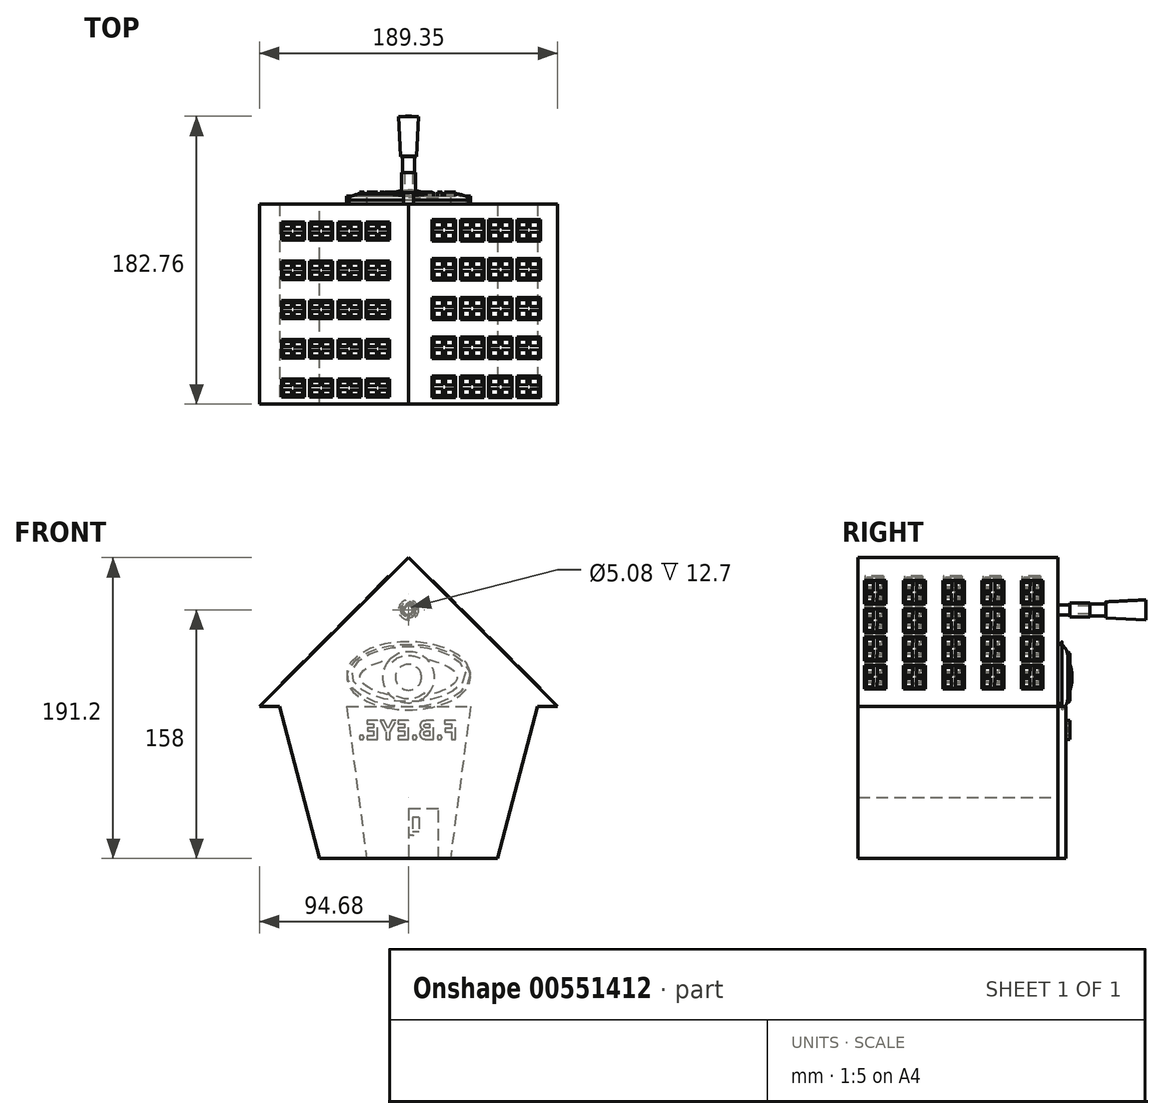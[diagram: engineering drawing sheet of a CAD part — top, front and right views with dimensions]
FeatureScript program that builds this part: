
annotation { "Feature Type Name" : "Feature", "Feature Type Description" : "" }
export const myFeature = defineFeature(function(context is Context, id is Id, definition is map)
    precondition{}
    {
        {
            var Q0;
            Q0=qCreatedBy(makeId("Front.planeOp"),FACE);
            var sketch = newSketch(context, id + "F0", { "sketchPlane" : qUnion([Q0])});
            skLineSegment(sketch, "E0.bottom", {"start": v(-42.95, 48.23) * mm, "end": v(35.63, 48.23) * mm});
            skLineSegment(sketch, "E1.top", {"start": v(-30.23, -48.3) * mm, "end": v(22.9, -48.3) * mm});
            skLineSegment(sketch, "E2", {"start": v(35.63, 48.23) * mm, "end": v(22.9, -48.3) * mm});
            skLineSegment(sketch, "E3", {"start": v(-42.95, 48.23) * mm, "end": v(-30.23, -48.3) * mm});
            skLineSegment(sketch, "E4", {"start": v(-42.95, 48.23) * mm, "end": v(22.9, -48.3) * mm, "construction": true});
            skLineSegment(sketch, "E5", {"start": v(-30.23, -48.3) * mm, "end": v(35.63, 48.23) * mm, "construction": true});
            skLineSegment(sketch, "E6", {"start": v(-3.66, -48.3) * mm, "end": v(-3.66, 48.23) * mm, "construction": true});
            skLineSegment(sketch, "E7", {"start": v(-3.66, 68.9) * mm, "end": v(12.85, 68.9) * mm, "construction": true});
            skCircle(sketch, "E8", {"center": v(-3.66, 68.9) * mm, "radius": 16.51 * mm});
            skLineSegment(sketch, "E9", {"start": v(-42.95, 48.23) * mm, "end": v(-42.95, 68.9) * mm, "construction": true});
            skLineSegment(sketch, "E10", {"start": v(35.63, 48.23) * mm, "end": v(35.63, 68.9) * mm, "construction": true});
            skEllipse(sketch, "E11", {"center": v(-3.66, 68.9) * mm, "majorRadius": 39.29 * mm, "minorRadius": 20.66 * mm, "majorAxis": v(1, 0)});
            skPoint(sketch, "E12", {"position": v(4.6, 68.9) * mm});
            skCircle(sketch, "E13", {"center": v(-3.66, 68.9) * mm, "radius": 8.26 * mm});
            skLineSegment(sketch, "E14", {"start": v(-3.66, 68.9) * mm, "end": v(-3.66, 66.88) * mm, "construction": true});
            skSolve(sketch);
        }
        {
            var Q0;
            Q0=makeQuery(id+"F0.imprint","IMPRINT",FACE,{"disambiguationData":[TD([[makeQuery(id+"F0.imprint","IMPRINT",EDGE,{"derivedFrom":sQuery(id+"F0.wireOp",EDGE,"E8")}),-1.0]])]});
            extrude(context, id + "F1", {"entities" : qUnion([Q0]), "oppositeDirection" : true, "depth" : 3.8 * mm, "offsetDistance" : 25.4 * mm});
        }
        {
            var Q0;
            Q0=makeQuery(id+"F0.imprint","IMPRINT",FACE,{"disambiguationData":[TD([[makeQuery(id+"F0.imprint","IMPRINT",EDGE,{"derivedFrom":sQuery(id+"F0.wireOp",EDGE,"E8")}),1.0]])]});
            extrude(context, id + "F2", {"entities" : qUnion([Q0]), "operationType" : NewBodyOperationType.ADD, "oppositeDirection" : true, "depth" : 5.08 * mm, "offsetDistance" : 25.4 * mm});
        }
        {
            var Q0;
            Q0=makeQuery(id+"F1.opExtrude","CAP_EDGE",EDGE,{"disambiguationData":[OSD([sQuery(id+"F0.wireOp",EDGE,"E11")])],"isStart":false});
            fillet(context, id + "F3", {"entities" : qUnion([Q0]), "radius" : 10.74 * mm, "tangentPropagation" : true, "allowEdgeOverflow" : false});
        }
        {
            var Q0;
            Q0=makeQuery(id+"F2.opExtrude","CAP_EDGE",EDGE,{"disambiguationData":[OSD([sQuery(id+"F0.wireOp",EDGE,"E8")])],"isStart":false});
            fillet(context, id + "F4", {"entities" : qUnion([Q0]), "radius" : 2.72 * mm, "tangentPropagation" : true, "allowEdgeOverflow" : false});
        }
        {
            var Q0;
            Q0=makeQuery(id+"F0.imprint","IMPRINT",FACE,{"disambiguationData":[TD([[makeQuery(id+"F0.imprint","IMPRINT",EDGE,{"derivedFrom":sQuery(id+"F0.wireOp",EDGE,"E13")}),1.0]])]});
            extrude(context, id + "F5", {"entities" : qUnion([Q0]), "operationType" : NewBodyOperationType.ADD, "oppositeDirection" : true, "depth" : 6.33 * mm, "offsetDistance" : 25.4 * mm});
        }
        {
            var Q0;
            Q0=makeQuery(id+"F5.opExtrude","CAP_FACE",FACE,{"disambiguationData":[OSD([sQuery(id+"F0.wireOp",EDGE,"E13")])],"isStart":false});
            fillet(context, id + "F6", {"entities" : qUnion([Q0]), "radius" : 26.1 * mm, "tangentPropagation" : true, "allowEdgeOverflow" : false});
        }
        {
            var Q0;
            Q0=makeQuery(id+"F0.imprint","IMPRINT",FACE,{"disambiguationData":[TD([[makeQuery(id+"F0.imprint","IMPRINT",EDGE,{"derivedFrom":sQuery(id+"F0.wireOp",EDGE,"E1.top")}),1.0]])]});
            extrude(context, id + "F7", {"entities" : qUnion([Q0]), "oppositeDirection" : true, "depth" : 5.08 * mm, "offsetDistance" : 25.4 * mm, "symmetric" : true});
        }
        {
            var Q0;
            Q0=makeQuery(id+"F0.imprint","IMPRINT",FACE,{"disambiguationData":[TD([[makeQuery(id+"F0.imprint","IMPRINT",EDGE,{"derivedFrom":sQuery(id+"F0.wireOp",EDGE,"E8")}),-1.0]])]});
            var Q1;
            Q1=makeQuery(id+"F0.imprint","IMPRINT",FACE,{"disambiguationData":[TD([[makeQuery(id+"F0.imprint","IMPRINT",EDGE,{"derivedFrom":sQuery(id+"F0.wireOp",EDGE,"E13")}),1.0]])]});
            var Q2;
            Q2=makeQuery(id+"F0.imprint","IMPRINT",FACE,{"disambiguationData":[TD([[makeQuery(id+"F0.imprint","IMPRINT",EDGE,{"derivedFrom":sQuery(id+"F0.wireOp",EDGE,"E8")}),1.0]])]});
            extrude(context, id + "F8", {"entities" : qUnion([Q0, Q1, Q2]), "depth" : 3.8 * mm, "offsetDistance" : 25.4 * mm});
        }
        {
            var Q0;
            Q0=makeQuery(id+"F8.opExtrude","CAP_EDGE",EDGE,{"disambiguationData":[OSD([sQuery(id+"F0.wireOp",EDGE,"E11")])],"isStart":false});
            fillet(context, id + "F9", {"entities" : qUnion([Q0]), "radius" : 10.33 * mm, "tangentPropagation" : true, "allowEdgeOverflow" : false});
        }
        {
            var Q0;
            Q0=makeQuery(id+"F1.opExtrude","SWEPT_BODY",BODY,{"disambiguationData":[OSD([sQuery(id+"F0.wireOp",EDGE,"E8"),sQuery(id+"F0.wireOp",EDGE,"E11")])]});
            var Q1;
            Q1=sQuery(id+"F0.wireOp",EDGE,"E14");
            transform(context, id + "F10", {"entities" : qUnion([Q0]), "transformType" : TransformType.TRANSLATION_ENTITY, "oppositeDirectionEntity" : false, "transformLine" : qUnion([Q1]), "makeCopy" : false});
        }
        {
            var Q0;
            Q0=makeQuery(id+"F7.opExtrude","CAP_FACE",FACE,{"disambiguationData":[OSD([sQuery(id+"F0.wireOp",EDGE,"E0.bottom"),sQuery(id+"F0.wireOp",EDGE,"E1.top"),sQuery(id+"F0.wireOp",EDGE,"E2"),sQuery(id+"F0.wireOp",EDGE,"E3")])],"isStart":false});
            var sketch = newSketch(context, id + "F11", { "sketchPlane" : qUnion([Q0])});
            skText(sketch, "E15", { "text": "F.B.EYE.", "fontName": "OpenSans-Bold.ttf"});
            const initialGuessF11  = {"E15": [-0.02755, 0.0275, 1, 0, 0.01194]};
            skSetInitialGuess(sketch, initialGuessF11);
            skSolve(sketch);
        }
        {
            var Q0;
            Q0=qSketchRegion(id+"F11",true);
            extrude(context, id + "F12", {"entities" : qUnion([Q0]), "operationType" : NewBodyOperationType.ADD, "depth" : 2.54 * mm, "offsetDistance" : 25.4 * mm});
        }
        {
            var Q0;
            Q0=makeQuery(id+"F7.opExtrude","CAP_FACE",FACE,{"disambiguationData":[OSD([sQuery(id+"F0.wireOp",EDGE,"E0.bottom"),sQuery(id+"F0.wireOp",EDGE,"E1.top"),sQuery(id+"F0.wireOp",EDGE,"E2"),sQuery(id+"F0.wireOp",EDGE,"E3")])],"isStart":true});
            var sketch = newSketch(context, id + "F13", { "sketchPlane" : qUnion([Q0])});
            skLineSegment(sketch, "E16.top", {"start": v(-85.64, -48.3) * mm, "end": v(78.31, -48.3) * mm});
            skLineSegment(sketch, "E16.left", {"start": v(-85.64, 48.23) * mm, "end": v(-85.64, -48.3) * mm});
            skLineSegment(sketch, "E16.right", {"start": v(78.31, 48.23) * mm, "end": v(78.31, -48.3) * mm});
            skPoint(sketch, "E17", {"position": v(-3.66, 43.57) * mm});
            skLineSegment(sketch, "E18.0", {"start": v(-42.95, 48.23) * mm, "end": v(22.9, -48.3) * mm});
            skLineSegment(sketch, "E19.0", {"start": v(-30.23, -48.3) * mm, "end": v(35.63, 48.23) * mm});
            skPoint(sketch, "E20", {"position": v(-3.66, -9.35) * mm});
            skLineSegment(sketch, "E21", {"start": v(-3.66, 43.57) * mm, "end": v(-3.66, -48.3) * mm});
            skLineSegment(sketch, "E22", {"start": v(-85.64, 48.23) * mm, "end": v(-98.34, 48.23) * mm});
            skLineSegment(sketch, "E23", {"start": v(-98.34, 48.23) * mm, "end": v(-3.66, 142.9) * mm});
            skLineSegment(sketch, "E24", {"start": v(-3.66, 142.9) * mm, "end": v(91.01, 48.23) * mm});
            skLineSegment(sketch, "E25", {"start": v(78.31, 48.23) * mm, "end": v(91.01, 48.23) * mm});
            skSolve(sketch);
        }
        {
            var Q0;
            Q0=qSketchRegion(id+"F13",true);
            extrude(context, id + "F14", {"entities" : qUnion([Q0]), "operationType" : NewBodyOperationType.ADD, "depth" : 127 * mm, "offsetDistance" : 25.4 * mm});
        }
        {
            var Q0;
            Q0=makeQuery(id+"F14.opExtrude","SWEPT_EDGE",EDGE,{"disambiguationData":[OSD([sQuery(id+"F13.wireOp",EDGE,"E16.top"),sQuery(id+"F13.wireOp",EDGE,"E16.left")])]});
            var Q1;
            Q1=makeQuery(id+"F14.opExtrude","SWEPT_EDGE",EDGE,{"disambiguationData":[OSD([sQuery(id+"F13.wireOp",EDGE,"E16.top"),sQuery(id+"F13.wireOp",EDGE,"E16.right")])]});
            chamfer(context, id + "F15", {"entities" : qUnion([Q0, Q1]), "chamferType" : ChamferType.OFFSET_ANGLE, "width" : 25.4 * mm, "oppositeDirection" : false, "angle" : 75.26 * degree, "tangentPropagation" : true});
        }
        {
            var Q0;
            Q0=makeQuery(id+"F14.opExtrude","SWEPT_FACE",FACE,{"disambiguationData":[OSD([sQuery(id+"F13.wireOp",EDGE,"E24")])]});
            var sketch = newSketch(context, id + "F16", { "sketchPlane" : qUnion([Q0])});
            skLineSegment(sketch, "E26.bottom", {"start": v(-124.24, 5.02) * mm, "end": v(-119.76, 5.02) * mm});
            skLineSegment(sketch, "E26.top", {"start": v(-124.24, -13.15) * mm, "end": v(-120.07, -13.15) * mm});
            skLineSegment(sketch, "E26.left", {"start": v(-124.24, 5.02) * mm, "end": v(-124.24, -2.98) * mm});
            skLineSegment(sketch, "E26.right", {"start": v(-113.04, 5.02) * mm, "end": v(-113.04, -2.98) * mm});
            skPoint(sketch, "E27", {"position": v(-118.64, -4.07) * mm});
            skPoint(sketch, "E27.positionSnap0", {"position": v(-113.04, -4.07) * mm});
            skPoint(sketch, "E27.positionSnap1", {"position": v(-118.64, -13.15) * mm});
            skLineSegment(sketch, "E28.left", {"start": v(-117.22, 5.02) * mm, "end": v(-117.36, -2.98) * mm});
            skLineSegment(sketch, "E28.right", {"start": v(-119.76, 5.02) * mm, "end": v(-119.9, -2.98) * mm});
            skLineSegment(sketch, "E29.bottom", {"start": v(-113.04, -5.15) * mm, "end": v(-117.4, -5.15) * mm});
            skLineSegment(sketch, "E29.top", {"start": v(-113.04, -2.98) * mm, "end": v(-117.36, -2.98) * mm});
            skLineSegment(sketch, "E30.0", {"start": v(-125.51, 6.29) * mm, "end": v(-111.77, 6.29) * mm});
            skLineSegment(sketch, "E30.1", {"start": v(-125.51, 6.29) * mm, "end": v(-125.51, -14.42) * mm});
            skLineSegment(sketch, "E30.2", {"start": v(-125.51, -14.42) * mm, "end": v(-111.77, -14.42) * mm});
            skLineSegment(sketch, "E30.3", {"start": v(-111.77, 6.29) * mm, "end": v(-111.77, -14.42) * mm});
            skLineSegment(sketch, "E31.trimOffspring", {"start": v(-119.9, -2.98) * mm, "end": v(-124.24, -2.98) * mm});
            skLineSegment(sketch, "E32.trimOffspring", {"start": v(-119.93, -5.15) * mm, "end": v(-120.07, -13.15) * mm});
            skLineSegment(sketch, "E33.trimOffspring", {"start": v(-119.93, -5.15) * mm, "end": v(-124.24, -5.15) * mm});
            skLineSegment(sketch, "E34.trimOffspring", {"start": v(-117.4, -5.15) * mm, "end": v(-117.53, -13.15) * mm});
            skLineSegment(sketch, "E35.trimOffspring", {"start": v(-113.04, -5.15) * mm, "end": v(-113.04, -13.15) * mm});
            skLineSegment(sketch, "E36.trimOffspring", {"start": v(-117.53, -13.15) * mm, "end": v(-113.04, -13.15) * mm});
            skLineSegment(sketch, "E37.trimOffspring", {"start": v(-124.24, -5.15) * mm, "end": v(-124.24, -13.15) * mm});
            skLineSegment(sketch, "E38.trimOffspring", {"start": v(-117.22, 5.02) * mm, "end": v(-113.04, 5.02) * mm});
            skPoint(sketch, "E39.0.1.0", {"position": v(-118.64, 21.33) * mm});
            skLineSegment(sketch, "E39.0.1.1", {"start": v(-117.22, 30.42) * mm, "end": v(-113.04, 30.42) * mm});
            skLineSegment(sketch, "E39.0.1.2", {"start": v(-113.04, 20.25) * mm, "end": v(-113.04, 12.25) * mm});
            skLineSegment(sketch, "E39.0.1.3", {"start": v(-117.53, 12.25) * mm, "end": v(-113.04, 12.25) * mm});
            skLineSegment(sketch, "E39.0.1.4", {"start": v(-125.51, 10.98) * mm, "end": v(-111.77, 10.98) * mm});
            skLineSegment(sketch, "E39.0.1.5", {"start": v(-125.51, 31.69) * mm, "end": v(-125.51, 10.98) * mm});
            skLineSegment(sketch, "E39.0.1.6", {"start": v(-113.04, 22.42) * mm, "end": v(-117.36, 22.42) * mm});
            skLineSegment(sketch, "E39.0.1.7", {"start": v(-113.04, 20.25) * mm, "end": v(-117.4, 20.25) * mm});
            skLineSegment(sketch, "E39.0.1.8", {"start": v(-119.76, 30.42) * mm, "end": v(-119.9, 22.42) * mm});
            skLineSegment(sketch, "E39.0.1.9", {"start": v(-117.22, 30.42) * mm, "end": v(-117.36, 22.42) * mm});
            skLineSegment(sketch, "E39.0.1.10", {"start": v(-113.04, 30.42) * mm, "end": v(-113.04, 22.42) * mm});
            skLineSegment(sketch, "E39.0.1.11", {"start": v(-124.24, 30.42) * mm, "end": v(-124.24, 22.42) * mm});
            skLineSegment(sketch, "E39.0.1.12", {"start": v(-124.24, 12.25) * mm, "end": v(-120.07, 12.25) * mm});
            skLineSegment(sketch, "E39.0.1.13", {"start": v(-124.24, 30.42) * mm, "end": v(-119.76, 30.42) * mm});
            skLineSegment(sketch, "E39.0.1.14", {"start": v(-117.4, 20.25) * mm, "end": v(-117.53, 12.25) * mm});
            skLineSegment(sketch, "E39.0.1.15", {"start": v(-119.93, 20.25) * mm, "end": v(-124.24, 20.25) * mm});
            skLineSegment(sketch, "E39.0.1.16", {"start": v(-119.93, 20.25) * mm, "end": v(-120.07, 12.25) * mm});
            skLineSegment(sketch, "E39.0.1.17", {"start": v(-125.51, 31.69) * mm, "end": v(-111.77, 31.69) * mm});
            skLineSegment(sketch, "E39.0.1.18", {"start": v(-111.77, 31.69) * mm, "end": v(-111.77, 10.98) * mm});
            skLineSegment(sketch, "E39.0.1.19", {"start": v(-119.9, 22.42) * mm, "end": v(-124.24, 22.42) * mm});
            skPoint(sketch, "E39.0.1.20", {"position": v(-113.04, 21.33) * mm});
            skPoint(sketch, "E39.0.1.21", {"position": v(-118.64, 12.25) * mm});
            skLineSegment(sketch, "E39.0.1.22", {"start": v(-124.24, 20.25) * mm, "end": v(-124.24, 12.25) * mm});
            skPoint(sketch, "E39.0.1.23", {"position": v(-118.64, 21.33) * mm});
            skPoint(sketch, "E39.0.1.24", {"position": v(-118.64, 21.33) * mm});
            skPoint(sketch, "E39.0.2.0", {"position": v(-118.64, 46.73) * mm});
            skLineSegment(sketch, "E39.0.2.1", {"start": v(-117.22, 55.82) * mm, "end": v(-113.04, 55.82) * mm});
            skLineSegment(sketch, "E39.0.2.2", {"start": v(-113.04, 45.65) * mm, "end": v(-113.04, 37.65) * mm});
            skLineSegment(sketch, "E39.0.2.3", {"start": v(-117.53, 37.65) * mm, "end": v(-113.04, 37.65) * mm});
            skLineSegment(sketch, "E39.0.2.4", {"start": v(-125.51, 36.38) * mm, "end": v(-111.77, 36.38) * mm});
            skLineSegment(sketch, "E39.0.2.5", {"start": v(-125.51, 57.09) * mm, "end": v(-125.51, 36.38) * mm});
            skLineSegment(sketch, "E39.0.2.6", {"start": v(-113.04, 47.82) * mm, "end": v(-117.36, 47.82) * mm});
            skLineSegment(sketch, "E39.0.2.7", {"start": v(-113.04, 45.65) * mm, "end": v(-117.4, 45.65) * mm});
            skLineSegment(sketch, "E39.0.2.8", {"start": v(-119.76, 55.82) * mm, "end": v(-119.9, 47.82) * mm});
            skLineSegment(sketch, "E39.0.2.9", {"start": v(-117.22, 55.82) * mm, "end": v(-117.36, 47.82) * mm});
            skLineSegment(sketch, "E39.0.2.10", {"start": v(-113.04, 55.82) * mm, "end": v(-113.04, 47.82) * mm});
            skLineSegment(sketch, "E39.0.2.11", {"start": v(-124.24, 55.82) * mm, "end": v(-124.24, 47.82) * mm});
            skLineSegment(sketch, "E39.0.2.12", {"start": v(-124.24, 37.65) * mm, "end": v(-120.07, 37.65) * mm});
            skLineSegment(sketch, "E39.0.2.13", {"start": v(-124.24, 55.82) * mm, "end": v(-119.76, 55.82) * mm});
            skLineSegment(sketch, "E39.0.2.14", {"start": v(-117.4, 45.65) * mm, "end": v(-117.53, 37.65) * mm});
            skLineSegment(sketch, "E39.0.2.15", {"start": v(-119.93, 45.65) * mm, "end": v(-124.24, 45.65) * mm});
            skLineSegment(sketch, "E39.0.2.16", {"start": v(-119.93, 45.65) * mm, "end": v(-120.07, 37.65) * mm});
            skLineSegment(sketch, "E39.0.2.17", {"start": v(-125.51, 57.09) * mm, "end": v(-111.77, 57.09) * mm});
            skLineSegment(sketch, "E39.0.2.18", {"start": v(-111.77, 57.09) * mm, "end": v(-111.77, 36.38) * mm});
            skLineSegment(sketch, "E39.0.2.19", {"start": v(-119.9, 47.82) * mm, "end": v(-124.24, 47.82) * mm});
            skPoint(sketch, "E39.0.2.20", {"position": v(-113.04, 46.73) * mm});
            skPoint(sketch, "E39.0.2.21", {"position": v(-118.64, 37.65) * mm});
            skLineSegment(sketch, "E39.0.2.22", {"start": v(-124.24, 45.65) * mm, "end": v(-124.24, 37.65) * mm});
            skPoint(sketch, "E39.0.2.23", {"position": v(-118.64, 46.73) * mm});
            skPoint(sketch, "E39.0.2.24", {"position": v(-118.64, 46.73) * mm});
            skPoint(sketch, "E39.0.3.0", {"position": v(-118.64, 72.13) * mm});
            skLineSegment(sketch, "E39.0.3.1", {"start": v(-117.22, 81.22) * mm, "end": v(-113.04, 81.22) * mm});
            skLineSegment(sketch, "E39.0.3.2", {"start": v(-113.04, 71.05) * mm, "end": v(-113.04, 63.05) * mm});
            skLineSegment(sketch, "E39.0.3.3", {"start": v(-117.53, 63.05) * mm, "end": v(-113.04, 63.05) * mm});
            skLineSegment(sketch, "E39.0.3.4", {"start": v(-125.51, 61.78) * mm, "end": v(-111.77, 61.78) * mm});
            skLineSegment(sketch, "E39.0.3.5", {"start": v(-125.51, 82.49) * mm, "end": v(-125.51, 61.78) * mm});
            skLineSegment(sketch, "E39.0.3.6", {"start": v(-113.04, 73.22) * mm, "end": v(-117.36, 73.22) * mm});
            skLineSegment(sketch, "E39.0.3.7", {"start": v(-113.04, 71.05) * mm, "end": v(-117.4, 71.05) * mm});
            skLineSegment(sketch, "E39.0.3.8", {"start": v(-119.76, 81.22) * mm, "end": v(-119.9, 73.22) * mm});
            skLineSegment(sketch, "E39.0.3.9", {"start": v(-117.22, 81.22) * mm, "end": v(-117.36, 73.22) * mm});
            skLineSegment(sketch, "E39.0.3.10", {"start": v(-113.04, 81.22) * mm, "end": v(-113.04, 73.22) * mm});
            skLineSegment(sketch, "E39.0.3.11", {"start": v(-124.24, 81.22) * mm, "end": v(-124.24, 73.22) * mm});
            skLineSegment(sketch, "E39.0.3.12", {"start": v(-124.24, 63.05) * mm, "end": v(-120.07, 63.05) * mm});
            skLineSegment(sketch, "E39.0.3.13", {"start": v(-124.24, 81.22) * mm, "end": v(-119.76, 81.22) * mm});
            skLineSegment(sketch, "E39.0.3.14", {"start": v(-117.4, 71.05) * mm, "end": v(-117.53, 63.05) * mm});
            skLineSegment(sketch, "E39.0.3.15", {"start": v(-119.93, 71.05) * mm, "end": v(-124.24, 71.05) * mm});
            skLineSegment(sketch, "E39.0.3.16", {"start": v(-119.93, 71.05) * mm, "end": v(-120.07, 63.05) * mm});
            skLineSegment(sketch, "E39.0.3.17", {"start": v(-125.51, 82.49) * mm, "end": v(-111.77, 82.49) * mm});
            skLineSegment(sketch, "E39.0.3.18", {"start": v(-111.77, 82.49) * mm, "end": v(-111.77, 61.78) * mm});
            skLineSegment(sketch, "E39.0.3.19", {"start": v(-119.9, 73.22) * mm, "end": v(-124.24, 73.22) * mm});
            skPoint(sketch, "E39.0.3.20", {"position": v(-113.04, 72.13) * mm});
            skPoint(sketch, "E39.0.3.21", {"position": v(-118.64, 63.05) * mm});
            skLineSegment(sketch, "E39.0.3.22", {"start": v(-124.24, 71.05) * mm, "end": v(-124.24, 63.05) * mm});
            skPoint(sketch, "E39.0.3.23", {"position": v(-118.64, 72.13) * mm});
            skPoint(sketch, "E39.0.3.24", {"position": v(-118.64, 72.13) * mm});
            skPoint(sketch, "E39.1.0.0", {"position": v(-93.75, -4.07) * mm});
            skLineSegment(sketch, "E39.1.0.1", {"start": v(-92.33, 5.02) * mm, "end": v(-88.15, 5.02) * mm});
            skLineSegment(sketch, "E39.1.0.2", {"start": v(-88.15, -5.15) * mm, "end": v(-88.15, -13.15) * mm});
            skLineSegment(sketch, "E39.1.0.3", {"start": v(-92.64, -13.15) * mm, "end": v(-88.15, -13.15) * mm});
            skLineSegment(sketch, "E39.1.0.4", {"start": v(-100.62, -14.42) * mm, "end": v(-86.88, -14.42) * mm});
            skLineSegment(sketch, "E39.1.0.5", {"start": v(-100.62, 6.29) * mm, "end": v(-100.62, -14.42) * mm});
            skLineSegment(sketch, "E39.1.0.6", {"start": v(-88.15, -2.98) * mm, "end": v(-92.47, -2.98) * mm});
            skLineSegment(sketch, "E39.1.0.7", {"start": v(-88.15, -5.15) * mm, "end": v(-92.5, -5.15) * mm});
            skLineSegment(sketch, "E39.1.0.8", {"start": v(-94.87, 5.02) * mm, "end": v(-95, -2.98) * mm});
            skLineSegment(sketch, "E39.1.0.9", {"start": v(-92.33, 5.02) * mm, "end": v(-92.47, -2.98) * mm});
            skLineSegment(sketch, "E39.1.0.10", {"start": v(-88.15, 5.02) * mm, "end": v(-88.15, -2.98) * mm});
            skLineSegment(sketch, "E39.1.0.11", {"start": v(-99.35, 5.02) * mm, "end": v(-99.35, -2.98) * mm});
            skLineSegment(sketch, "E39.1.0.12", {"start": v(-99.35, -13.15) * mm, "end": v(-95.17, -13.15) * mm});
            skLineSegment(sketch, "E39.1.0.13", {"start": v(-99.35, 5.02) * mm, "end": v(-94.87, 5.02) * mm});
            skLineSegment(sketch, "E39.1.0.14", {"start": v(-92.5, -5.15) * mm, "end": v(-92.64, -13.15) * mm});
            skLineSegment(sketch, "E39.1.0.15", {"start": v(-95.04, -5.15) * mm, "end": v(-99.35, -5.15) * mm});
            skLineSegment(sketch, "E39.1.0.16", {"start": v(-95.04, -5.15) * mm, "end": v(-95.17, -13.15) * mm});
            skLineSegment(sketch, "E39.1.0.17", {"start": v(-100.62, 6.29) * mm, "end": v(-86.88, 6.29) * mm});
            skLineSegment(sketch, "E39.1.0.18", {"start": v(-86.88, 6.29) * mm, "end": v(-86.88, -14.42) * mm});
            skLineSegment(sketch, "E39.1.0.19", {"start": v(-95, -2.98) * mm, "end": v(-99.35, -2.98) * mm});
            skPoint(sketch, "E39.1.0.20", {"position": v(-88.15, -4.07) * mm});
            skPoint(sketch, "E39.1.0.21", {"position": v(-93.75, -13.15) * mm});
            skLineSegment(sketch, "E39.1.0.22", {"start": v(-99.35, -5.15) * mm, "end": v(-99.35, -13.15) * mm});
            skPoint(sketch, "E39.1.0.23", {"position": v(-93.75, -4.07) * mm});
            skPoint(sketch, "E39.1.0.24", {"position": v(-93.75, -4.07) * mm});
            skPoint(sketch, "E39.1.1.0", {"position": v(-93.75, 21.33) * mm});
            skLineSegment(sketch, "E39.1.1.1", {"start": v(-92.33, 30.42) * mm, "end": v(-88.15, 30.42) * mm});
            skLineSegment(sketch, "E39.1.1.2", {"start": v(-88.15, 20.25) * mm, "end": v(-88.15, 12.25) * mm});
            skLineSegment(sketch, "E39.1.1.3", {"start": v(-92.64, 12.25) * mm, "end": v(-88.15, 12.25) * mm});
            skLineSegment(sketch, "E39.1.1.4", {"start": v(-100.62, 10.98) * mm, "end": v(-86.88, 10.98) * mm});
            skLineSegment(sketch, "E39.1.1.5", {"start": v(-100.62, 31.69) * mm, "end": v(-100.62, 10.98) * mm});
            skLineSegment(sketch, "E39.1.1.6", {"start": v(-88.15, 22.42) * mm, "end": v(-92.47, 22.42) * mm});
            skLineSegment(sketch, "E39.1.1.7", {"start": v(-88.15, 20.25) * mm, "end": v(-92.5, 20.25) * mm});
            skLineSegment(sketch, "E39.1.1.8", {"start": v(-94.87, 30.42) * mm, "end": v(-95, 22.42) * mm});
            skLineSegment(sketch, "E39.1.1.9", {"start": v(-92.33, 30.42) * mm, "end": v(-92.47, 22.42) * mm});
            skLineSegment(sketch, "E39.1.1.10", {"start": v(-88.15, 30.42) * mm, "end": v(-88.15, 22.42) * mm});
            skLineSegment(sketch, "E39.1.1.11", {"start": v(-99.35, 30.42) * mm, "end": v(-99.35, 22.42) * mm});
            skLineSegment(sketch, "E39.1.1.12", {"start": v(-99.35, 12.25) * mm, "end": v(-95.17, 12.25) * mm});
            skLineSegment(sketch, "E39.1.1.13", {"start": v(-99.35, 30.42) * mm, "end": v(-94.87, 30.42) * mm});
            skLineSegment(sketch, "E39.1.1.14", {"start": v(-92.5, 20.25) * mm, "end": v(-92.64, 12.25) * mm});
            skLineSegment(sketch, "E39.1.1.15", {"start": v(-95.04, 20.25) * mm, "end": v(-99.35, 20.25) * mm});
            skLineSegment(sketch, "E39.1.1.16", {"start": v(-95.04, 20.25) * mm, "end": v(-95.17, 12.25) * mm});
            skLineSegment(sketch, "E39.1.1.17", {"start": v(-100.62, 31.69) * mm, "end": v(-86.88, 31.69) * mm});
            skLineSegment(sketch, "E39.1.1.18", {"start": v(-86.88, 31.69) * mm, "end": v(-86.88, 10.98) * mm});
            skLineSegment(sketch, "E39.1.1.19", {"start": v(-95, 22.42) * mm, "end": v(-99.35, 22.42) * mm});
            skPoint(sketch, "E39.1.1.20", {"position": v(-88.15, 21.33) * mm});
            skPoint(sketch, "E39.1.1.21", {"position": v(-93.75, 12.25) * mm});
            skLineSegment(sketch, "E39.1.1.22", {"start": v(-99.35, 20.25) * mm, "end": v(-99.35, 12.25) * mm});
            skPoint(sketch, "E39.1.1.23", {"position": v(-93.75, 21.33) * mm});
            skPoint(sketch, "E39.1.1.24", {"position": v(-93.75, 21.33) * mm});
            skPoint(sketch, "E39.1.2.0", {"position": v(-93.75, 46.73) * mm});
            skLineSegment(sketch, "E39.1.2.1", {"start": v(-92.33, 55.82) * mm, "end": v(-88.15, 55.82) * mm});
            skLineSegment(sketch, "E39.1.2.2", {"start": v(-88.15, 45.65) * mm, "end": v(-88.15, 37.65) * mm});
            skLineSegment(sketch, "E39.1.2.3", {"start": v(-92.64, 37.65) * mm, "end": v(-88.15, 37.65) * mm});
            skLineSegment(sketch, "E39.1.2.4", {"start": v(-100.62, 36.38) * mm, "end": v(-86.88, 36.38) * mm});
            skLineSegment(sketch, "E39.1.2.5", {"start": v(-100.62, 57.09) * mm, "end": v(-100.62, 36.38) * mm});
            skLineSegment(sketch, "E39.1.2.6", {"start": v(-88.15, 47.82) * mm, "end": v(-92.47, 47.82) * mm});
            skLineSegment(sketch, "E39.1.2.7", {"start": v(-88.15, 45.65) * mm, "end": v(-92.5, 45.65) * mm});
            skLineSegment(sketch, "E39.1.2.8", {"start": v(-94.87, 55.82) * mm, "end": v(-95, 47.82) * mm});
            skLineSegment(sketch, "E39.1.2.9", {"start": v(-92.33, 55.82) * mm, "end": v(-92.47, 47.82) * mm});
            skLineSegment(sketch, "E39.1.2.10", {"start": v(-88.15, 55.82) * mm, "end": v(-88.15, 47.82) * mm});
            skLineSegment(sketch, "E39.1.2.11", {"start": v(-99.35, 55.82) * mm, "end": v(-99.35, 47.82) * mm});
            skLineSegment(sketch, "E39.1.2.12", {"start": v(-99.35, 37.65) * mm, "end": v(-95.17, 37.65) * mm});
            skLineSegment(sketch, "E39.1.2.13", {"start": v(-99.35, 55.82) * mm, "end": v(-94.87, 55.82) * mm});
            skLineSegment(sketch, "E39.1.2.14", {"start": v(-92.5, 45.65) * mm, "end": v(-92.64, 37.65) * mm});
            skLineSegment(sketch, "E39.1.2.15", {"start": v(-95.04, 45.65) * mm, "end": v(-99.35, 45.65) * mm});
            skLineSegment(sketch, "E39.1.2.16", {"start": v(-95.04, 45.65) * mm, "end": v(-95.17, 37.65) * mm});
            skLineSegment(sketch, "E39.1.2.17", {"start": v(-100.62, 57.09) * mm, "end": v(-86.88, 57.09) * mm});
            skLineSegment(sketch, "E39.1.2.18", {"start": v(-86.88, 57.09) * mm, "end": v(-86.88, 36.38) * mm});
            skLineSegment(sketch, "E39.1.2.19", {"start": v(-95, 47.82) * mm, "end": v(-99.35, 47.82) * mm});
            skPoint(sketch, "E39.1.2.20", {"position": v(-88.15, 46.73) * mm});
            skPoint(sketch, "E39.1.2.21", {"position": v(-93.75, 37.65) * mm});
            skLineSegment(sketch, "E39.1.2.22", {"start": v(-99.35, 45.65) * mm, "end": v(-99.35, 37.65) * mm});
            skPoint(sketch, "E39.1.2.23", {"position": v(-93.75, 46.73) * mm});
            skPoint(sketch, "E39.1.2.24", {"position": v(-93.75, 46.73) * mm});
            skPoint(sketch, "E39.1.3.0", {"position": v(-93.75, 72.13) * mm});
            skLineSegment(sketch, "E39.1.3.1", {"start": v(-92.33, 81.22) * mm, "end": v(-88.15, 81.22) * mm});
            skLineSegment(sketch, "E39.1.3.2", {"start": v(-88.15, 71.05) * mm, "end": v(-88.15, 63.05) * mm});
            skLineSegment(sketch, "E39.1.3.3", {"start": v(-92.64, 63.05) * mm, "end": v(-88.15, 63.05) * mm});
            skLineSegment(sketch, "E39.1.3.4", {"start": v(-100.62, 61.78) * mm, "end": v(-86.88, 61.78) * mm});
            skLineSegment(sketch, "E39.1.3.5", {"start": v(-100.62, 82.49) * mm, "end": v(-100.62, 61.78) * mm});
            skLineSegment(sketch, "E39.1.3.6", {"start": v(-88.15, 73.22) * mm, "end": v(-92.47, 73.22) * mm});
            skLineSegment(sketch, "E39.1.3.7", {"start": v(-88.15, 71.05) * mm, "end": v(-92.5, 71.05) * mm});
            skLineSegment(sketch, "E39.1.3.8", {"start": v(-94.87, 81.22) * mm, "end": v(-95, 73.22) * mm});
            skLineSegment(sketch, "E39.1.3.9", {"start": v(-92.33, 81.22) * mm, "end": v(-92.47, 73.22) * mm});
            skLineSegment(sketch, "E39.1.3.10", {"start": v(-88.15, 81.22) * mm, "end": v(-88.15, 73.22) * mm});
            skLineSegment(sketch, "E39.1.3.11", {"start": v(-99.35, 81.22) * mm, "end": v(-99.35, 73.22) * mm});
            skLineSegment(sketch, "E39.1.3.12", {"start": v(-99.35, 63.05) * mm, "end": v(-95.17, 63.05) * mm});
            skLineSegment(sketch, "E39.1.3.13", {"start": v(-99.35, 81.22) * mm, "end": v(-94.87, 81.22) * mm});
            skLineSegment(sketch, "E39.1.3.14", {"start": v(-92.5, 71.05) * mm, "end": v(-92.64, 63.05) * mm});
            skLineSegment(sketch, "E39.1.3.15", {"start": v(-95.04, 71.05) * mm, "end": v(-99.35, 71.05) * mm});
            skLineSegment(sketch, "E39.1.3.16", {"start": v(-95.04, 71.05) * mm, "end": v(-95.17, 63.05) * mm});
            skLineSegment(sketch, "E39.1.3.17", {"start": v(-100.62, 82.49) * mm, "end": v(-86.88, 82.49) * mm});
            skLineSegment(sketch, "E39.1.3.18", {"start": v(-86.88, 82.49) * mm, "end": v(-86.88, 61.78) * mm});
            skLineSegment(sketch, "E39.1.3.19", {"start": v(-95, 73.22) * mm, "end": v(-99.35, 73.22) * mm});
            skPoint(sketch, "E39.1.3.20", {"position": v(-88.15, 72.13) * mm});
            skPoint(sketch, "E39.1.3.21", {"position": v(-93.75, 63.05) * mm});
            skLineSegment(sketch, "E39.1.3.22", {"start": v(-99.35, 71.05) * mm, "end": v(-99.35, 63.05) * mm});
            skPoint(sketch, "E39.1.3.23", {"position": v(-93.75, 72.13) * mm});
            skPoint(sketch, "E39.1.3.24", {"position": v(-93.75, 72.13) * mm});
            skPoint(sketch, "E39.2.0.0", {"position": v(-68.86, -4.07) * mm});
            skLineSegment(sketch, "E39.2.0.1", {"start": v(-67.44, 5.02) * mm, "end": v(-63.26, 5.02) * mm});
            skLineSegment(sketch, "E39.2.0.2", {"start": v(-63.26, -5.15) * mm, "end": v(-63.26, -13.15) * mm});
            skLineSegment(sketch, "E39.2.0.3", {"start": v(-67.75, -13.15) * mm, "end": v(-63.26, -13.15) * mm});
            skLineSegment(sketch, "E39.2.0.4", {"start": v(-75.73, -14.42) * mm, "end": v(-62, -14.42) * mm});
            skLineSegment(sketch, "E39.2.0.5", {"start": v(-75.73, 6.29) * mm, "end": v(-75.73, -14.42) * mm});
            skLineSegment(sketch, "E39.2.0.6", {"start": v(-63.26, -2.98) * mm, "end": v(-67.57, -2.98) * mm});
            skLineSegment(sketch, "E39.2.0.7", {"start": v(-63.26, -5.15) * mm, "end": v(-67.61, -5.15) * mm});
            skLineSegment(sketch, "E39.2.0.8", {"start": v(-69.97, 5.02) * mm, "end": v(-70.1, -2.98) * mm});
            skLineSegment(sketch, "E39.2.0.9", {"start": v(-67.44, 5.02) * mm, "end": v(-67.57, -2.98) * mm});
            skLineSegment(sketch, "E39.2.0.10", {"start": v(-63.26, 5.02) * mm, "end": v(-63.26, -2.98) * mm});
            skLineSegment(sketch, "E39.2.0.11", {"start": v(-74.46, 5.02) * mm, "end": v(-74.46, -2.98) * mm});
            skLineSegment(sketch, "E39.2.0.12", {"start": v(-74.46, -13.15) * mm, "end": v(-70.28, -13.15) * mm});
            skLineSegment(sketch, "E39.2.0.13", {"start": v(-74.46, 5.02) * mm, "end": v(-69.97, 5.02) * mm});
            skLineSegment(sketch, "E39.2.0.14", {"start": v(-67.61, -5.15) * mm, "end": v(-67.75, -13.15) * mm});
            skLineSegment(sketch, "E39.2.0.15", {"start": v(-70.15, -5.15) * mm, "end": v(-74.46, -5.15) * mm});
            skLineSegment(sketch, "E39.2.0.16", {"start": v(-70.15, -5.15) * mm, "end": v(-70.28, -13.15) * mm});
            skLineSegment(sketch, "E39.2.0.17", {"start": v(-75.73, 6.29) * mm, "end": v(-62, 6.29) * mm});
            skLineSegment(sketch, "E39.2.0.18", {"start": v(-62, 6.29) * mm, "end": v(-62, -14.42) * mm});
            skLineSegment(sketch, "E39.2.0.19", {"start": v(-70.1, -2.98) * mm, "end": v(-74.46, -2.98) * mm});
            skPoint(sketch, "E39.2.0.20", {"position": v(-63.26, -4.07) * mm});
            skPoint(sketch, "E39.2.0.21", {"position": v(-68.86, -13.15) * mm});
            skLineSegment(sketch, "E39.2.0.22", {"start": v(-74.46, -5.15) * mm, "end": v(-74.46, -13.15) * mm});
            skPoint(sketch, "E39.2.0.23", {"position": v(-68.86, -4.07) * mm});
            skPoint(sketch, "E39.2.0.24", {"position": v(-68.86, -4.07) * mm});
            skPoint(sketch, "E39.2.1.0", {"position": v(-68.86, 21.33) * mm});
            skLineSegment(sketch, "E39.2.1.1", {"start": v(-67.44, 30.42) * mm, "end": v(-63.26, 30.42) * mm});
            skLineSegment(sketch, "E39.2.1.2", {"start": v(-63.26, 20.25) * mm, "end": v(-63.26, 12.25) * mm});
            skLineSegment(sketch, "E39.2.1.3", {"start": v(-67.75, 12.25) * mm, "end": v(-63.26, 12.25) * mm});
            skLineSegment(sketch, "E39.2.1.4", {"start": v(-75.73, 10.98) * mm, "end": v(-62, 10.98) * mm});
            skLineSegment(sketch, "E39.2.1.5", {"start": v(-75.73, 31.69) * mm, "end": v(-75.73, 10.98) * mm});
            skLineSegment(sketch, "E39.2.1.6", {"start": v(-63.26, 22.42) * mm, "end": v(-67.57, 22.42) * mm});
            skLineSegment(sketch, "E39.2.1.7", {"start": v(-63.26, 20.25) * mm, "end": v(-67.61, 20.25) * mm});
            skLineSegment(sketch, "E39.2.1.8", {"start": v(-69.97, 30.42) * mm, "end": v(-70.1, 22.42) * mm});
            skLineSegment(sketch, "E39.2.1.9", {"start": v(-67.44, 30.42) * mm, "end": v(-67.57, 22.42) * mm});
            skLineSegment(sketch, "E39.2.1.10", {"start": v(-63.26, 30.42) * mm, "end": v(-63.26, 22.42) * mm});
            skLineSegment(sketch, "E39.2.1.11", {"start": v(-74.46, 30.42) * mm, "end": v(-74.46, 22.42) * mm});
            skLineSegment(sketch, "E39.2.1.12", {"start": v(-74.46, 12.25) * mm, "end": v(-70.28, 12.25) * mm});
            skLineSegment(sketch, "E39.2.1.13", {"start": v(-74.46, 30.42) * mm, "end": v(-69.97, 30.42) * mm});
            skLineSegment(sketch, "E39.2.1.14", {"start": v(-67.61, 20.25) * mm, "end": v(-67.75, 12.25) * mm});
            skLineSegment(sketch, "E39.2.1.15", {"start": v(-70.15, 20.25) * mm, "end": v(-74.46, 20.25) * mm});
            skLineSegment(sketch, "E39.2.1.16", {"start": v(-70.15, 20.25) * mm, "end": v(-70.28, 12.25) * mm});
            skLineSegment(sketch, "E39.2.1.17", {"start": v(-75.73, 31.69) * mm, "end": v(-62, 31.69) * mm});
            skLineSegment(sketch, "E39.2.1.18", {"start": v(-62, 31.69) * mm, "end": v(-62, 10.98) * mm});
            skLineSegment(sketch, "E39.2.1.19", {"start": v(-70.1, 22.42) * mm, "end": v(-74.46, 22.42) * mm});
            skPoint(sketch, "E39.2.1.20", {"position": v(-63.26, 21.33) * mm});
            skPoint(sketch, "E39.2.1.21", {"position": v(-68.86, 12.25) * mm});
            skLineSegment(sketch, "E39.2.1.22", {"start": v(-74.46, 20.25) * mm, "end": v(-74.46, 12.25) * mm});
            skPoint(sketch, "E39.2.1.23", {"position": v(-68.86, 21.33) * mm});
            skPoint(sketch, "E39.2.1.24", {"position": v(-68.86, 21.33) * mm});
            skPoint(sketch, "E39.2.2.0", {"position": v(-68.86, 46.73) * mm});
            skLineSegment(sketch, "E39.2.2.1", {"start": v(-67.44, 55.82) * mm, "end": v(-63.26, 55.82) * mm});
            skLineSegment(sketch, "E39.2.2.2", {"start": v(-63.26, 45.65) * mm, "end": v(-63.26, 37.65) * mm});
            skLineSegment(sketch, "E39.2.2.3", {"start": v(-67.75, 37.65) * mm, "end": v(-63.26, 37.65) * mm});
            skLineSegment(sketch, "E39.2.2.4", {"start": v(-75.73, 36.38) * mm, "end": v(-62, 36.38) * mm});
            skLineSegment(sketch, "E39.2.2.5", {"start": v(-75.73, 57.09) * mm, "end": v(-75.73, 36.38) * mm});
            skLineSegment(sketch, "E39.2.2.6", {"start": v(-63.26, 47.82) * mm, "end": v(-67.57, 47.82) * mm});
            skLineSegment(sketch, "E39.2.2.7", {"start": v(-63.26, 45.65) * mm, "end": v(-67.61, 45.65) * mm});
            skLineSegment(sketch, "E39.2.2.8", {"start": v(-69.97, 55.82) * mm, "end": v(-70.1, 47.82) * mm});
            skLineSegment(sketch, "E39.2.2.9", {"start": v(-67.44, 55.82) * mm, "end": v(-67.57, 47.82) * mm});
            skLineSegment(sketch, "E39.2.2.10", {"start": v(-63.26, 55.82) * mm, "end": v(-63.26, 47.82) * mm});
            skLineSegment(sketch, "E39.2.2.11", {"start": v(-74.46, 55.82) * mm, "end": v(-74.46, 47.82) * mm});
            skLineSegment(sketch, "E39.2.2.12", {"start": v(-74.46, 37.65) * mm, "end": v(-70.28, 37.65) * mm});
            skLineSegment(sketch, "E39.2.2.13", {"start": v(-74.46, 55.82) * mm, "end": v(-69.97, 55.82) * mm});
            skLineSegment(sketch, "E39.2.2.14", {"start": v(-67.61, 45.65) * mm, "end": v(-67.75, 37.65) * mm});
            skLineSegment(sketch, "E39.2.2.15", {"start": v(-70.15, 45.65) * mm, "end": v(-74.46, 45.65) * mm});
            skLineSegment(sketch, "E39.2.2.16", {"start": v(-70.15, 45.65) * mm, "end": v(-70.28, 37.65) * mm});
            skLineSegment(sketch, "E39.2.2.17", {"start": v(-75.73, 57.09) * mm, "end": v(-62, 57.09) * mm});
            skLineSegment(sketch, "E39.2.2.18", {"start": v(-62, 57.09) * mm, "end": v(-62, 36.38) * mm});
            skLineSegment(sketch, "E39.2.2.19", {"start": v(-70.1, 47.82) * mm, "end": v(-74.46, 47.82) * mm});
            skPoint(sketch, "E39.2.2.20", {"position": v(-63.26, 46.73) * mm});
            skPoint(sketch, "E39.2.2.21", {"position": v(-68.86, 37.65) * mm});
            skLineSegment(sketch, "E39.2.2.22", {"start": v(-74.46, 45.65) * mm, "end": v(-74.46, 37.65) * mm});
            skPoint(sketch, "E39.2.2.23", {"position": v(-68.86, 46.73) * mm});
            skPoint(sketch, "E39.2.2.24", {"position": v(-68.86, 46.73) * mm});
            skPoint(sketch, "E39.2.3.0", {"position": v(-68.86, 72.13) * mm});
            skLineSegment(sketch, "E39.2.3.1", {"start": v(-67.44, 81.22) * mm, "end": v(-63.26, 81.22) * mm});
            skLineSegment(sketch, "E39.2.3.2", {"start": v(-63.26, 71.05) * mm, "end": v(-63.26, 63.05) * mm});
            skLineSegment(sketch, "E39.2.3.3", {"start": v(-67.75, 63.05) * mm, "end": v(-63.26, 63.05) * mm});
            skLineSegment(sketch, "E39.2.3.4", {"start": v(-75.73, 61.78) * mm, "end": v(-62, 61.78) * mm});
            skLineSegment(sketch, "E39.2.3.5", {"start": v(-75.73, 82.49) * mm, "end": v(-75.73, 61.78) * mm});
            skLineSegment(sketch, "E39.2.3.6", {"start": v(-63.26, 73.22) * mm, "end": v(-67.57, 73.22) * mm});
            skLineSegment(sketch, "E39.2.3.7", {"start": v(-63.26, 71.05) * mm, "end": v(-67.61, 71.05) * mm});
            skLineSegment(sketch, "E39.2.3.8", {"start": v(-69.97, 81.22) * mm, "end": v(-70.1, 73.22) * mm});
            skLineSegment(sketch, "E39.2.3.9", {"start": v(-67.44, 81.22) * mm, "end": v(-67.57, 73.22) * mm});
            skLineSegment(sketch, "E39.2.3.10", {"start": v(-63.26, 81.22) * mm, "end": v(-63.26, 73.22) * mm});
            skLineSegment(sketch, "E39.2.3.11", {"start": v(-74.46, 81.22) * mm, "end": v(-74.46, 73.22) * mm});
            skLineSegment(sketch, "E39.2.3.12", {"start": v(-74.46, 63.05) * mm, "end": v(-70.28, 63.05) * mm});
            skLineSegment(sketch, "E39.2.3.13", {"start": v(-74.46, 81.22) * mm, "end": v(-69.97, 81.22) * mm});
            skLineSegment(sketch, "E39.2.3.14", {"start": v(-67.61, 71.05) * mm, "end": v(-67.75, 63.05) * mm});
            skLineSegment(sketch, "E39.2.3.15", {"start": v(-70.15, 71.05) * mm, "end": v(-74.46, 71.05) * mm});
            skLineSegment(sketch, "E39.2.3.16", {"start": v(-70.15, 71.05) * mm, "end": v(-70.28, 63.05) * mm});
            skLineSegment(sketch, "E39.2.3.17", {"start": v(-75.73, 82.49) * mm, "end": v(-62, 82.49) * mm});
            skLineSegment(sketch, "E39.2.3.18", {"start": v(-62, 82.49) * mm, "end": v(-62, 61.78) * mm});
            skLineSegment(sketch, "E39.2.3.19", {"start": v(-70.1, 73.22) * mm, "end": v(-74.46, 73.22) * mm});
            skPoint(sketch, "E39.2.3.20", {"position": v(-63.26, 72.13) * mm});
            skPoint(sketch, "E39.2.3.21", {"position": v(-68.86, 63.05) * mm});
            skLineSegment(sketch, "E39.2.3.22", {"start": v(-74.46, 71.05) * mm, "end": v(-74.46, 63.05) * mm});
            skPoint(sketch, "E39.2.3.23", {"position": v(-68.86, 72.13) * mm});
            skPoint(sketch, "E39.2.3.24", {"position": v(-68.86, 72.13) * mm});
            skPoint(sketch, "E39.3.0.0", {"position": v(-43.97, -4.07) * mm});
            skLineSegment(sketch, "E39.3.0.1", {"start": v(-42.55, 5.02) * mm, "end": v(-38.37, 5.02) * mm});
            skLineSegment(sketch, "E39.3.0.2", {"start": v(-38.37, -5.15) * mm, "end": v(-38.37, -13.15) * mm});
            skLineSegment(sketch, "E39.3.0.3", {"start": v(-42.85, -13.15) * mm, "end": v(-38.37, -13.15) * mm});
            skLineSegment(sketch, "E39.3.0.4", {"start": v(-50.84, -14.42) * mm, "end": v(-37.1, -14.42) * mm});
            skLineSegment(sketch, "E39.3.0.5", {"start": v(-50.84, 6.29) * mm, "end": v(-50.84, -14.42) * mm});
            skLineSegment(sketch, "E39.3.0.6", {"start": v(-38.37, -2.98) * mm, "end": v(-42.68, -2.98) * mm});
            skLineSegment(sketch, "E39.3.0.7", {"start": v(-38.37, -5.15) * mm, "end": v(-42.72, -5.15) * mm});
            skLineSegment(sketch, "E39.3.0.8", {"start": v(-45.08, 5.02) * mm, "end": v(-45.22, -2.98) * mm});
            skLineSegment(sketch, "E39.3.0.9", {"start": v(-42.55, 5.02) * mm, "end": v(-42.68, -2.98) * mm});
            skLineSegment(sketch, "E39.3.0.10", {"start": v(-38.37, 5.02) * mm, "end": v(-38.37, -2.98) * mm});
            skLineSegment(sketch, "E39.3.0.11", {"start": v(-49.57, 5.02) * mm, "end": v(-49.57, -2.98) * mm});
            skLineSegment(sketch, "E39.3.0.12", {"start": v(-49.57, -13.15) * mm, "end": v(-45.39, -13.15) * mm});
            skLineSegment(sketch, "E39.3.0.13", {"start": v(-49.57, 5.02) * mm, "end": v(-45.08, 5.02) * mm});
            skLineSegment(sketch, "E39.3.0.14", {"start": v(-42.72, -5.15) * mm, "end": v(-42.85, -13.15) * mm});
            skLineSegment(sketch, "E39.3.0.15", {"start": v(-45.25, -5.15) * mm, "end": v(-49.57, -5.15) * mm});
            skLineSegment(sketch, "E39.3.0.16", {"start": v(-45.25, -5.15) * mm, "end": v(-45.39, -13.15) * mm});
            skLineSegment(sketch, "E39.3.0.17", {"start": v(-50.84, 6.29) * mm, "end": v(-37.1, 6.29) * mm});
            skLineSegment(sketch, "E39.3.0.18", {"start": v(-37.1, 6.29) * mm, "end": v(-37.1, -14.42) * mm});
            skLineSegment(sketch, "E39.3.0.19", {"start": v(-45.22, -2.98) * mm, "end": v(-49.57, -2.98) * mm});
            skPoint(sketch, "E39.3.0.20", {"position": v(-38.37, -4.07) * mm});
            skPoint(sketch, "E39.3.0.21", {"position": v(-43.97, -13.15) * mm});
            skLineSegment(sketch, "E39.3.0.22", {"start": v(-49.57, -5.15) * mm, "end": v(-49.57, -13.15) * mm});
            skPoint(sketch, "E39.3.0.23", {"position": v(-43.97, -4.07) * mm});
            skPoint(sketch, "E39.3.0.24", {"position": v(-43.97, -4.07) * mm});
            skPoint(sketch, "E39.3.1.0", {"position": v(-43.97, 21.33) * mm});
            skLineSegment(sketch, "E39.3.1.1", {"start": v(-42.55, 30.42) * mm, "end": v(-38.37, 30.42) * mm});
            skLineSegment(sketch, "E39.3.1.2", {"start": v(-38.37, 20.25) * mm, "end": v(-38.37, 12.25) * mm});
            skLineSegment(sketch, "E39.3.1.3", {"start": v(-42.85, 12.25) * mm, "end": v(-38.37, 12.25) * mm});
            skLineSegment(sketch, "E39.3.1.4", {"start": v(-50.84, 10.98) * mm, "end": v(-37.1, 10.98) * mm});
            skLineSegment(sketch, "E39.3.1.5", {"start": v(-50.84, 31.69) * mm, "end": v(-50.84, 10.98) * mm});
            skLineSegment(sketch, "E39.3.1.6", {"start": v(-38.37, 22.42) * mm, "end": v(-42.68, 22.42) * mm});
            skLineSegment(sketch, "E39.3.1.7", {"start": v(-38.37, 20.25) * mm, "end": v(-42.72, 20.25) * mm});
            skLineSegment(sketch, "E39.3.1.8", {"start": v(-45.08, 30.42) * mm, "end": v(-45.22, 22.42) * mm});
            skLineSegment(sketch, "E39.3.1.9", {"start": v(-42.55, 30.42) * mm, "end": v(-42.68, 22.42) * mm});
            skLineSegment(sketch, "E39.3.1.10", {"start": v(-38.37, 30.42) * mm, "end": v(-38.37, 22.42) * mm});
            skLineSegment(sketch, "E39.3.1.11", {"start": v(-49.57, 30.42) * mm, "end": v(-49.57, 22.42) * mm});
            skLineSegment(sketch, "E39.3.1.12", {"start": v(-49.57, 12.25) * mm, "end": v(-45.39, 12.25) * mm});
            skLineSegment(sketch, "E39.3.1.13", {"start": v(-49.57, 30.42) * mm, "end": v(-45.08, 30.42) * mm});
            skLineSegment(sketch, "E39.3.1.14", {"start": v(-42.72, 20.25) * mm, "end": v(-42.85, 12.25) * mm});
            skLineSegment(sketch, "E39.3.1.15", {"start": v(-45.25, 20.25) * mm, "end": v(-49.57, 20.25) * mm});
            skLineSegment(sketch, "E39.3.1.16", {"start": v(-45.25, 20.25) * mm, "end": v(-45.39, 12.25) * mm});
            skLineSegment(sketch, "E39.3.1.17", {"start": v(-50.84, 31.69) * mm, "end": v(-37.1, 31.69) * mm});
            skLineSegment(sketch, "E39.3.1.18", {"start": v(-37.1, 31.69) * mm, "end": v(-37.1, 10.98) * mm});
            skLineSegment(sketch, "E39.3.1.19", {"start": v(-45.22, 22.42) * mm, "end": v(-49.57, 22.42) * mm});
            skPoint(sketch, "E39.3.1.20", {"position": v(-38.37, 21.33) * mm});
            skPoint(sketch, "E39.3.1.21", {"position": v(-43.97, 12.25) * mm});
            skLineSegment(sketch, "E39.3.1.22", {"start": v(-49.57, 20.25) * mm, "end": v(-49.57, 12.25) * mm});
            skPoint(sketch, "E39.3.1.23", {"position": v(-43.97, 21.33) * mm});
            skPoint(sketch, "E39.3.1.24", {"position": v(-43.97, 21.33) * mm});
            skPoint(sketch, "E39.3.2.0", {"position": v(-43.97, 46.73) * mm});
            skLineSegment(sketch, "E39.3.2.1", {"start": v(-42.55, 55.82) * mm, "end": v(-38.37, 55.82) * mm});
            skLineSegment(sketch, "E39.3.2.2", {"start": v(-38.37, 45.65) * mm, "end": v(-38.37, 37.65) * mm});
            skLineSegment(sketch, "E39.3.2.3", {"start": v(-42.85, 37.65) * mm, "end": v(-38.37, 37.65) * mm});
            skLineSegment(sketch, "E39.3.2.4", {"start": v(-50.84, 36.38) * mm, "end": v(-37.1, 36.38) * mm});
            skLineSegment(sketch, "E39.3.2.5", {"start": v(-50.84, 57.09) * mm, "end": v(-50.84, 36.38) * mm});
            skLineSegment(sketch, "E39.3.2.6", {"start": v(-38.37, 47.82) * mm, "end": v(-42.68, 47.82) * mm});
            skLineSegment(sketch, "E39.3.2.7", {"start": v(-38.37, 45.65) * mm, "end": v(-42.72, 45.65) * mm});
            skLineSegment(sketch, "E39.3.2.8", {"start": v(-45.08, 55.82) * mm, "end": v(-45.22, 47.82) * mm});
            skLineSegment(sketch, "E39.3.2.9", {"start": v(-42.55, 55.82) * mm, "end": v(-42.68, 47.82) * mm});
            skLineSegment(sketch, "E39.3.2.10", {"start": v(-38.37, 55.82) * mm, "end": v(-38.37, 47.82) * mm});
            skLineSegment(sketch, "E39.3.2.11", {"start": v(-49.57, 55.82) * mm, "end": v(-49.57, 47.82) * mm});
            skLineSegment(sketch, "E39.3.2.12", {"start": v(-49.57, 37.65) * mm, "end": v(-45.39, 37.65) * mm});
            skLineSegment(sketch, "E39.3.2.13", {"start": v(-49.57, 55.82) * mm, "end": v(-45.08, 55.82) * mm});
            skLineSegment(sketch, "E39.3.2.14", {"start": v(-42.72, 45.65) * mm, "end": v(-42.85, 37.65) * mm});
            skLineSegment(sketch, "E39.3.2.15", {"start": v(-45.25, 45.65) * mm, "end": v(-49.57, 45.65) * mm});
            skLineSegment(sketch, "E39.3.2.16", {"start": v(-45.25, 45.65) * mm, "end": v(-45.39, 37.65) * mm});
            skLineSegment(sketch, "E39.3.2.17", {"start": v(-50.84, 57.09) * mm, "end": v(-37.1, 57.09) * mm});
            skLineSegment(sketch, "E39.3.2.18", {"start": v(-37.1, 57.09) * mm, "end": v(-37.1, 36.38) * mm});
            skLineSegment(sketch, "E39.3.2.19", {"start": v(-45.22, 47.82) * mm, "end": v(-49.57, 47.82) * mm});
            skPoint(sketch, "E39.3.2.20", {"position": v(-38.37, 46.73) * mm});
            skPoint(sketch, "E39.3.2.21", {"position": v(-43.97, 37.65) * mm});
            skLineSegment(sketch, "E39.3.2.22", {"start": v(-49.57, 45.65) * mm, "end": v(-49.57, 37.65) * mm});
            skPoint(sketch, "E39.3.2.23", {"position": v(-43.97, 46.73) * mm});
            skPoint(sketch, "E39.3.2.24", {"position": v(-43.97, 46.73) * mm});
            skPoint(sketch, "E39.3.3.0", {"position": v(-43.97, 72.13) * mm});
            skLineSegment(sketch, "E39.3.3.1", {"start": v(-42.55, 81.22) * mm, "end": v(-38.37, 81.22) * mm});
            skLineSegment(sketch, "E39.3.3.2", {"start": v(-38.37, 71.05) * mm, "end": v(-38.37, 63.05) * mm});
            skLineSegment(sketch, "E39.3.3.3", {"start": v(-42.85, 63.05) * mm, "end": v(-38.37, 63.05) * mm});
            skLineSegment(sketch, "E39.3.3.4", {"start": v(-50.84, 61.78) * mm, "end": v(-37.1, 61.78) * mm});
            skLineSegment(sketch, "E39.3.3.5", {"start": v(-50.84, 82.49) * mm, "end": v(-50.84, 61.78) * mm});
            skLineSegment(sketch, "E39.3.3.6", {"start": v(-38.37, 73.22) * mm, "end": v(-42.68, 73.22) * mm});
            skLineSegment(sketch, "E39.3.3.7", {"start": v(-38.37, 71.05) * mm, "end": v(-42.72, 71.05) * mm});
            skLineSegment(sketch, "E39.3.3.8", {"start": v(-45.08, 81.22) * mm, "end": v(-45.22, 73.22) * mm});
            skLineSegment(sketch, "E39.3.3.9", {"start": v(-42.55, 81.22) * mm, "end": v(-42.68, 73.22) * mm});
            skLineSegment(sketch, "E39.3.3.10", {"start": v(-38.37, 81.22) * mm, "end": v(-38.37, 73.22) * mm});
            skLineSegment(sketch, "E39.3.3.11", {"start": v(-49.57, 81.22) * mm, "end": v(-49.57, 73.22) * mm});
            skLineSegment(sketch, "E39.3.3.12", {"start": v(-49.57, 63.05) * mm, "end": v(-45.39, 63.05) * mm});
            skLineSegment(sketch, "E39.3.3.13", {"start": v(-49.57, 81.22) * mm, "end": v(-45.08, 81.22) * mm});
            skLineSegment(sketch, "E39.3.3.14", {"start": v(-42.72, 71.05) * mm, "end": v(-42.85, 63.05) * mm});
            skLineSegment(sketch, "E39.3.3.15", {"start": v(-45.25, 71.05) * mm, "end": v(-49.57, 71.05) * mm});
            skLineSegment(sketch, "E39.3.3.16", {"start": v(-45.25, 71.05) * mm, "end": v(-45.39, 63.05) * mm});
            skLineSegment(sketch, "E39.3.3.17", {"start": v(-50.84, 82.49) * mm, "end": v(-37.1, 82.49) * mm});
            skLineSegment(sketch, "E39.3.3.18", {"start": v(-37.1, 82.49) * mm, "end": v(-37.1, 61.78) * mm});
            skLineSegment(sketch, "E39.3.3.19", {"start": v(-45.22, 73.22) * mm, "end": v(-49.57, 73.22) * mm});
            skPoint(sketch, "E39.3.3.20", {"position": v(-38.37, 72.13) * mm});
            skPoint(sketch, "E39.3.3.21", {"position": v(-43.97, 63.05) * mm});
            skLineSegment(sketch, "E39.3.3.22", {"start": v(-49.57, 71.05) * mm, "end": v(-49.57, 63.05) * mm});
            skPoint(sketch, "E39.3.3.23", {"position": v(-43.97, 72.13) * mm});
            skPoint(sketch, "E39.3.3.24", {"position": v(-43.97, 72.13) * mm});
            skPoint(sketch, "E39.4.0.0", {"position": v(-19.08, -4.07) * mm});
            skLineSegment(sketch, "E39.4.0.1", {"start": v(-17.66, 5.02) * mm, "end": v(-13.48, 5.02) * mm});
            skLineSegment(sketch, "E39.4.0.2", {"start": v(-13.48, -5.15) * mm, "end": v(-13.48, -13.15) * mm});
            skLineSegment(sketch, "E39.4.0.3", {"start": v(-17.96, -13.15) * mm, "end": v(-13.48, -13.15) * mm});
            skLineSegment(sketch, "E39.4.0.4", {"start": v(-25.95, -14.42) * mm, "end": v(-12.2, -14.42) * mm});
            skLineSegment(sketch, "E39.4.0.5", {"start": v(-25.95, 6.29) * mm, "end": v(-25.95, -14.42) * mm});
            skLineSegment(sketch, "E39.4.0.6", {"start": v(-13.48, -2.98) * mm, "end": v(-17.8, -2.98) * mm});
            skLineSegment(sketch, "E39.4.0.7", {"start": v(-13.48, -5.15) * mm, "end": v(-17.83, -5.15) * mm});
            skLineSegment(sketch, "E39.4.0.8", {"start": v(-20.2, 5.02) * mm, "end": v(-20.33, -2.98) * mm});
            skLineSegment(sketch, "E39.4.0.9", {"start": v(-17.66, 5.02) * mm, "end": v(-17.8, -2.98) * mm});
            skLineSegment(sketch, "E39.4.0.10", {"start": v(-13.48, 5.02) * mm, "end": v(-13.48, -2.98) * mm});
            skLineSegment(sketch, "E39.4.0.11", {"start": v(-24.68, 5.02) * mm, "end": v(-24.68, -2.98) * mm});
            skLineSegment(sketch, "E39.4.0.12", {"start": v(-24.68, -13.15) * mm, "end": v(-20.5, -13.15) * mm});
            skLineSegment(sketch, "E39.4.0.13", {"start": v(-24.68, 5.02) * mm, "end": v(-20.2, 5.02) * mm});
            skLineSegment(sketch, "E39.4.0.14", {"start": v(-17.83, -5.15) * mm, "end": v(-17.96, -13.15) * mm});
            skLineSegment(sketch, "E39.4.0.15", {"start": v(-20.36, -5.15) * mm, "end": v(-24.68, -5.15) * mm});
            skLineSegment(sketch, "E39.4.0.16", {"start": v(-20.36, -5.15) * mm, "end": v(-20.5, -13.15) * mm});
            skLineSegment(sketch, "E39.4.0.17", {"start": v(-25.95, 6.29) * mm, "end": v(-12.2, 6.29) * mm});
            skLineSegment(sketch, "E39.4.0.18", {"start": v(-12.2, 6.29) * mm, "end": v(-12.2, -14.42) * mm});
            skLineSegment(sketch, "E39.4.0.19", {"start": v(-20.33, -2.98) * mm, "end": v(-24.68, -2.98) * mm});
            skPoint(sketch, "E39.4.0.20", {"position": v(-13.48, -4.07) * mm});
            skPoint(sketch, "E39.4.0.21", {"position": v(-19.08, -13.15) * mm});
            skLineSegment(sketch, "E39.4.0.22", {"start": v(-24.68, -5.15) * mm, "end": v(-24.68, -13.15) * mm});
            skPoint(sketch, "E39.4.0.23", {"position": v(-19.08, -4.07) * mm});
            skPoint(sketch, "E39.4.0.24", {"position": v(-19.08, -4.07) * mm});
            skPoint(sketch, "E39.4.1.0", {"position": v(-19.08, 21.33) * mm});
            skLineSegment(sketch, "E39.4.1.1", {"start": v(-17.66, 30.42) * mm, "end": v(-13.48, 30.42) * mm});
            skLineSegment(sketch, "E39.4.1.2", {"start": v(-13.48, 20.25) * mm, "end": v(-13.48, 12.25) * mm});
            skLineSegment(sketch, "E39.4.1.3", {"start": v(-17.96, 12.25) * mm, "end": v(-13.48, 12.25) * mm});
            skLineSegment(sketch, "E39.4.1.4", {"start": v(-25.95, 10.98) * mm, "end": v(-12.2, 10.98) * mm});
            skLineSegment(sketch, "E39.4.1.5", {"start": v(-25.95, 31.69) * mm, "end": v(-25.95, 10.98) * mm});
            skLineSegment(sketch, "E39.4.1.6", {"start": v(-13.48, 22.42) * mm, "end": v(-17.8, 22.42) * mm});
            skLineSegment(sketch, "E39.4.1.7", {"start": v(-13.48, 20.25) * mm, "end": v(-17.83, 20.25) * mm});
            skLineSegment(sketch, "E39.4.1.8", {"start": v(-20.2, 30.42) * mm, "end": v(-20.33, 22.42) * mm});
            skLineSegment(sketch, "E39.4.1.9", {"start": v(-17.66, 30.42) * mm, "end": v(-17.8, 22.42) * mm});
            skLineSegment(sketch, "E39.4.1.10", {"start": v(-13.48, 30.42) * mm, "end": v(-13.48, 22.42) * mm});
            skLineSegment(sketch, "E39.4.1.11", {"start": v(-24.68, 30.42) * mm, "end": v(-24.68, 22.42) * mm});
            skLineSegment(sketch, "E39.4.1.12", {"start": v(-24.68, 12.25) * mm, "end": v(-20.5, 12.25) * mm});
            skLineSegment(sketch, "E39.4.1.13", {"start": v(-24.68, 30.42) * mm, "end": v(-20.2, 30.42) * mm});
            skLineSegment(sketch, "E39.4.1.14", {"start": v(-17.83, 20.25) * mm, "end": v(-17.96, 12.25) * mm});
            skLineSegment(sketch, "E39.4.1.15", {"start": v(-20.36, 20.25) * mm, "end": v(-24.68, 20.25) * mm});
            skLineSegment(sketch, "E39.4.1.16", {"start": v(-20.36, 20.25) * mm, "end": v(-20.5, 12.25) * mm});
            skLineSegment(sketch, "E39.4.1.17", {"start": v(-25.95, 31.69) * mm, "end": v(-12.2, 31.69) * mm});
            skLineSegment(sketch, "E39.4.1.18", {"start": v(-12.2, 31.69) * mm, "end": v(-12.2, 10.98) * mm});
            skLineSegment(sketch, "E39.4.1.19", {"start": v(-20.33, 22.42) * mm, "end": v(-24.68, 22.42) * mm});
            skPoint(sketch, "E39.4.1.20", {"position": v(-13.48, 21.33) * mm});
            skPoint(sketch, "E39.4.1.21", {"position": v(-19.08, 12.25) * mm});
            skLineSegment(sketch, "E39.4.1.22", {"start": v(-24.68, 20.25) * mm, "end": v(-24.68, 12.25) * mm});
            skPoint(sketch, "E39.4.1.23", {"position": v(-19.08, 21.33) * mm});
            skPoint(sketch, "E39.4.1.24", {"position": v(-19.08, 21.33) * mm});
            skPoint(sketch, "E39.4.2.0", {"position": v(-19.08, 46.73) * mm});
            skLineSegment(sketch, "E39.4.2.1", {"start": v(-17.66, 55.82) * mm, "end": v(-13.48, 55.82) * mm});
            skLineSegment(sketch, "E39.4.2.2", {"start": v(-13.48, 45.65) * mm, "end": v(-13.48, 37.65) * mm});
            skLineSegment(sketch, "E39.4.2.3", {"start": v(-17.96, 37.65) * mm, "end": v(-13.48, 37.65) * mm});
            skLineSegment(sketch, "E39.4.2.4", {"start": v(-25.95, 36.38) * mm, "end": v(-12.2, 36.38) * mm});
            skLineSegment(sketch, "E39.4.2.5", {"start": v(-25.95, 57.09) * mm, "end": v(-25.95, 36.38) * mm});
            skLineSegment(sketch, "E39.4.2.6", {"start": v(-13.48, 47.82) * mm, "end": v(-17.8, 47.82) * mm});
            skLineSegment(sketch, "E39.4.2.7", {"start": v(-13.48, 45.65) * mm, "end": v(-17.83, 45.65) * mm});
            skLineSegment(sketch, "E39.4.2.8", {"start": v(-20.2, 55.82) * mm, "end": v(-20.33, 47.82) * mm});
            skLineSegment(sketch, "E39.4.2.9", {"start": v(-17.66, 55.82) * mm, "end": v(-17.8, 47.82) * mm});
            skLineSegment(sketch, "E39.4.2.10", {"start": v(-13.48, 55.82) * mm, "end": v(-13.48, 47.82) * mm});
            skLineSegment(sketch, "E39.4.2.11", {"start": v(-24.68, 55.82) * mm, "end": v(-24.68, 47.82) * mm});
            skLineSegment(sketch, "E39.4.2.12", {"start": v(-24.68, 37.65) * mm, "end": v(-20.5, 37.65) * mm});
            skLineSegment(sketch, "E39.4.2.13", {"start": v(-24.68, 55.82) * mm, "end": v(-20.2, 55.82) * mm});
            skLineSegment(sketch, "E39.4.2.14", {"start": v(-17.83, 45.65) * mm, "end": v(-17.96, 37.65) * mm});
            skLineSegment(sketch, "E39.4.2.15", {"start": v(-20.36, 45.65) * mm, "end": v(-24.68, 45.65) * mm});
            skLineSegment(sketch, "E39.4.2.16", {"start": v(-20.36, 45.65) * mm, "end": v(-20.5, 37.65) * mm});
            skLineSegment(sketch, "E39.4.2.17", {"start": v(-25.95, 57.09) * mm, "end": v(-12.2, 57.09) * mm});
            skLineSegment(sketch, "E39.4.2.18", {"start": v(-12.2, 57.09) * mm, "end": v(-12.2, 36.38) * mm});
            skLineSegment(sketch, "E39.4.2.19", {"start": v(-20.33, 47.82) * mm, "end": v(-24.68, 47.82) * mm});
            skPoint(sketch, "E39.4.2.20", {"position": v(-13.48, 46.73) * mm});
            skPoint(sketch, "E39.4.2.21", {"position": v(-19.08, 37.65) * mm});
            skLineSegment(sketch, "E39.4.2.22", {"start": v(-24.68, 45.65) * mm, "end": v(-24.68, 37.65) * mm});
            skPoint(sketch, "E39.4.2.23", {"position": v(-19.08, 46.73) * mm});
            skPoint(sketch, "E39.4.2.24", {"position": v(-19.08, 46.73) * mm});
            skPoint(sketch, "E39.4.3.0", {"position": v(-19.08, 72.13) * mm});
            skLineSegment(sketch, "E39.4.3.1", {"start": v(-17.66, 81.22) * mm, "end": v(-13.48, 81.22) * mm});
            skLineSegment(sketch, "E39.4.3.2", {"start": v(-13.48, 71.05) * mm, "end": v(-13.48, 63.05) * mm});
            skLineSegment(sketch, "E39.4.3.3", {"start": v(-17.96, 63.05) * mm, "end": v(-13.48, 63.05) * mm});
            skLineSegment(sketch, "E39.4.3.4", {"start": v(-25.95, 61.78) * mm, "end": v(-12.2, 61.78) * mm});
            skLineSegment(sketch, "E39.4.3.5", {"start": v(-25.95, 82.49) * mm, "end": v(-25.95, 61.78) * mm});
            skLineSegment(sketch, "E39.4.3.6", {"start": v(-13.48, 73.22) * mm, "end": v(-17.8, 73.22) * mm});
            skLineSegment(sketch, "E39.4.3.7", {"start": v(-13.48, 71.05) * mm, "end": v(-17.83, 71.05) * mm});
            skLineSegment(sketch, "E39.4.3.8", {"start": v(-20.2, 81.22) * mm, "end": v(-20.33, 73.22) * mm});
            skLineSegment(sketch, "E39.4.3.9", {"start": v(-17.66, 81.22) * mm, "end": v(-17.8, 73.22) * mm});
            skLineSegment(sketch, "E39.4.3.10", {"start": v(-13.48, 81.22) * mm, "end": v(-13.48, 73.22) * mm});
            skLineSegment(sketch, "E39.4.3.11", {"start": v(-24.68, 81.22) * mm, "end": v(-24.68, 73.22) * mm});
            skLineSegment(sketch, "E39.4.3.12", {"start": v(-24.68, 63.05) * mm, "end": v(-20.5, 63.05) * mm});
            skLineSegment(sketch, "E39.4.3.13", {"start": v(-24.68, 81.22) * mm, "end": v(-20.2, 81.22) * mm});
            skLineSegment(sketch, "E39.4.3.14", {"start": v(-17.83, 71.05) * mm, "end": v(-17.96, 63.05) * mm});
            skLineSegment(sketch, "E39.4.3.15", {"start": v(-20.36, 71.05) * mm, "end": v(-24.68, 71.05) * mm});
            skLineSegment(sketch, "E39.4.3.16", {"start": v(-20.36, 71.05) * mm, "end": v(-20.5, 63.05) * mm});
            skLineSegment(sketch, "E39.4.3.17", {"start": v(-25.95, 82.49) * mm, "end": v(-12.2, 82.49) * mm});
            skLineSegment(sketch, "E39.4.3.18", {"start": v(-12.2, 82.49) * mm, "end": v(-12.2, 61.78) * mm});
            skLineSegment(sketch, "E39.4.3.19", {"start": v(-20.33, 73.22) * mm, "end": v(-24.68, 73.22) * mm});
            skPoint(sketch, "E39.4.3.20", {"position": v(-13.48, 72.13) * mm});
            skPoint(sketch, "E39.4.3.21", {"position": v(-19.08, 63.05) * mm});
            skLineSegment(sketch, "E39.4.3.22", {"start": v(-24.68, 71.05) * mm, "end": v(-24.68, 63.05) * mm});
            skPoint(sketch, "E39.4.3.23", {"position": v(-19.08, 72.13) * mm});
            skPoint(sketch, "E39.4.3.24", {"position": v(-19.08, 72.13) * mm});
            skLineSegment(sketch, "E39.direction1", {"start": v(-125.51, -14.42) * mm, "end": v(-100.62, -14.42) * mm, "construction": true});
            skLineSegment(sketch, "E39.direction2", {"start": v(-125.51, -14.42) * mm, "end": v(-125.51, 10.98) * mm, "construction": true});
            skSolve(sketch);
        }
        {
            var Q0;
            Q0=makeQuery(id+"F16.imprint","IMPRINT",FACE,{"disambiguationData":[TD([[makeQuery(id+"F16.imprint","IMPRINT",EDGE,{"derivedFrom":sQuery(id+"F16.wireOp",EDGE,"E26.bottom")}),1.0]])]});
            var Q1;
            Q1=makeQuery(id+"F16.imprint","IMPRINT",FACE,{"disambiguationData":[TD([[makeQuery(id+"F16.imprint","IMPRINT",EDGE,{"derivedFrom":sQuery(id+"F16.wireOp",EDGE,"E39.0.1.1")}),1.0]])]});
            var Q2;
            Q2=makeQuery(id+"F16.imprint","IMPRINT",FACE,{"disambiguationData":[TD([[makeQuery(id+"F16.imprint","IMPRINT",EDGE,{"derivedFrom":sQuery(id+"F16.wireOp",EDGE,"E39.0.2.1")}),1.0]])]});
            var Q3;
            Q3=makeQuery(id+"F16.imprint","IMPRINT",FACE,{"disambiguationData":[TD([[makeQuery(id+"F16.imprint","IMPRINT",EDGE,{"derivedFrom":sQuery(id+"F16.wireOp",EDGE,"E39.0.3.1")}),1.0]])]});
            var Q4;
            Q4=makeQuery(id+"F16.imprint","IMPRINT",FACE,{"disambiguationData":[TD([[makeQuery(id+"F16.imprint","IMPRINT",EDGE,{"derivedFrom":sQuery(id+"F16.wireOp",EDGE,"E39.1.3.1")}),1.0]])]});
            var Q5;
            Q5=makeQuery(id+"F16.imprint","IMPRINT",FACE,{"disambiguationData":[TD([[makeQuery(id+"F16.imprint","IMPRINT",EDGE,{"derivedFrom":sQuery(id+"F16.wireOp",EDGE,"E39.2.3.1")}),1.0]])]});
            var Q6;
            Q6=makeQuery(id+"F16.imprint","IMPRINT",FACE,{"disambiguationData":[TD([[makeQuery(id+"F16.imprint","IMPRINT",EDGE,{"derivedFrom":sQuery(id+"F16.wireOp",EDGE,"E39.3.3.1")}),1.0]])]});
            var Q7;
            Q7=makeQuery(id+"F16.imprint","IMPRINT",FACE,{"disambiguationData":[TD([[makeQuery(id+"F16.imprint","IMPRINT",EDGE,{"derivedFrom":sQuery(id+"F16.wireOp",EDGE,"E39.2.2.1")}),1.0]])]});
            var Q8;
            Q8=makeQuery(id+"F16.imprint","IMPRINT",FACE,{"disambiguationData":[TD([[makeQuery(id+"F16.imprint","IMPRINT",EDGE,{"derivedFrom":sQuery(id+"F16.wireOp",EDGE,"E39.1.2.1")}),1.0]])]});
            var Q9;
            Q9=makeQuery(id+"F16.imprint","IMPRINT",FACE,{"disambiguationData":[TD([[makeQuery(id+"F16.imprint","IMPRINT",EDGE,{"derivedFrom":sQuery(id+"F16.wireOp",EDGE,"E39.1.1.1")}),1.0]])]});
            var Q10;
            Q10=makeQuery(id+"F16.imprint","IMPRINT",FACE,{"disambiguationData":[TD([[makeQuery(id+"F16.imprint","IMPRINT",EDGE,{"derivedFrom":sQuery(id+"F16.wireOp",EDGE,"E39.2.1.1")}),1.0]])]});
            var Q11;
            Q11=makeQuery(id+"F16.imprint","IMPRINT",FACE,{"disambiguationData":[TD([[makeQuery(id+"F16.imprint","IMPRINT",EDGE,{"derivedFrom":sQuery(id+"F16.wireOp",EDGE,"E39.1.0.1")}),1.0]])]});
            var Q12;
            Q12=makeQuery(id+"F16.imprint","IMPRINT",FACE,{"disambiguationData":[TD([[makeQuery(id+"F16.imprint","IMPRINT",EDGE,{"derivedFrom":sQuery(id+"F16.wireOp",EDGE,"E39.2.0.1")}),1.0]])]});
            var Q13;
            Q13=makeQuery(id+"F16.imprint","IMPRINT",FACE,{"disambiguationData":[TD([[makeQuery(id+"F16.imprint","IMPRINT",EDGE,{"derivedFrom":sQuery(id+"F16.wireOp",EDGE,"E39.3.0.1")}),1.0]])]});
            var Q14;
            Q14=makeQuery(id+"F16.imprint","IMPRINT",FACE,{"disambiguationData":[TD([[makeQuery(id+"F16.imprint","IMPRINT",EDGE,{"derivedFrom":sQuery(id+"F16.wireOp",EDGE,"E39.4.0.1")}),1.0]])]});
            var Q15;
            Q15=makeQuery(id+"F16.imprint","IMPRINT",FACE,{"disambiguationData":[TD([[makeQuery(id+"F16.imprint","IMPRINT",EDGE,{"derivedFrom":sQuery(id+"F16.wireOp",EDGE,"E39.4.1.1")}),1.0]])]});
            var Q16;
            Q16=makeQuery(id+"F16.imprint","IMPRINT",FACE,{"disambiguationData":[TD([[makeQuery(id+"F16.imprint","IMPRINT",EDGE,{"derivedFrom":sQuery(id+"F16.wireOp",EDGE,"E39.3.1.1")}),1.0]])]});
            var Q17;
            Q17=makeQuery(id+"F16.imprint","IMPRINT",FACE,{"disambiguationData":[TD([[makeQuery(id+"F16.imprint","IMPRINT",EDGE,{"derivedFrom":sQuery(id+"F16.wireOp",EDGE,"E39.3.2.1")}),1.0]])]});
            var Q18;
            Q18=makeQuery(id+"F16.imprint","IMPRINT",FACE,{"disambiguationData":[TD([[makeQuery(id+"F16.imprint","IMPRINT",EDGE,{"derivedFrom":sQuery(id+"F16.wireOp",EDGE,"E39.4.2.1")}),1.0]])]});
            var Q19;
            Q19=makeQuery(id+"F16.imprint","IMPRINT",FACE,{"disambiguationData":[TD([[makeQuery(id+"F16.imprint","IMPRINT",EDGE,{"derivedFrom":sQuery(id+"F16.wireOp",EDGE,"E39.4.3.1")}),1.0]])]});
            extrude(context, id + "F17", {"entities" : qUnion([Q0, Q1, Q2, Q3, Q4, Q5, Q6, Q7, Q8, Q9, Q10, Q11, Q12, Q13, Q14, Q15, Q16, Q17, Q18, Q19]), "depth" : 0.5 * mm, "offsetDistance" : 25.4 * mm});
        }
        {
            var Q0;
            Q0=makeQuery(id+"F14.opExtrude","SWEPT_FACE",FACE,{"disambiguationData":[OSD([sQuery(id+"F13.wireOp",EDGE,"E23")])]});
            var sketch = newSketch(context, id + "F18", { "sketchPlane" : qUnion([Q0])});
            skLineSegment(sketch, "E40.bottom", {"start": v(15.18, 3.75) * mm, "end": v(18.6, 3.75) * mm});
            skLineSegment(sketch, "E40.top", {"start": v(15.18, -13.98) * mm, "end": v(18.35, -13.98) * mm});
            skLineSegment(sketch, "E40.left", {"start": v(15.18, 3.75) * mm, "end": v(15.18, -4.16) * mm});
            skLineSegment(sketch, "E40.right", {"start": v(24.25, 3.75) * mm, "end": v(24.25, -4.16) * mm});
            skPoint(sketch, "E41", {"position": v(19.72, -5.12) * mm});
            skPoint(sketch, "E41.positionSnap0", {"position": v(24.25, -5.12) * mm});
            skPoint(sketch, "E41.positionSnap1", {"position": v(19.72, -13.98) * mm});
            skLineSegment(sketch, "E42.left", {"start": v(21.08, 3.75) * mm, "end": v(20.97, -4.16) * mm});
            skLineSegment(sketch, "E42.right", {"start": v(18.6, 3.75) * mm, "end": v(18.49, -4.16) * mm});
            skLineSegment(sketch, "E43.bottom", {"start": v(24.25, -6.07) * mm, "end": v(20.95, -6.07) * mm});
            skLineSegment(sketch, "E43.top", {"start": v(24.25, -4.16) * mm, "end": v(20.97, -4.16) * mm});
            skLineSegment(sketch, "E44.0", {"start": v(13.9, 5.02) * mm, "end": v(25.52, 5.02) * mm});
            skLineSegment(sketch, "E44.1", {"start": v(13.9, 5.02) * mm, "end": v(13.9, -15.25) * mm});
            skLineSegment(sketch, "E44.2", {"start": v(13.9, -15.25) * mm, "end": v(25.52, -15.25) * mm});
            skLineSegment(sketch, "E44.3", {"start": v(25.52, 5.02) * mm, "end": v(25.52, -15.25) * mm});
            skLineSegment(sketch, "E45.trimOffspring", {"start": v(18.49, -4.16) * mm, "end": v(15.18, -4.16) * mm});
            skLineSegment(sketch, "E46.trimOffspring", {"start": v(18.46, -6.07) * mm, "end": v(18.35, -13.98) * mm});
            skLineSegment(sketch, "E47.trimOffspring", {"start": v(18.46, -6.07) * mm, "end": v(15.18, -6.07) * mm});
            skLineSegment(sketch, "E48.trimOffspring", {"start": v(20.95, -6.07) * mm, "end": v(20.84, -13.98) * mm});
            skLineSegment(sketch, "E49.trimOffspring", {"start": v(24.25, -6.07) * mm, "end": v(24.25, -13.98) * mm});
            skLineSegment(sketch, "E50.trimOffspring", {"start": v(20.84, -13.98) * mm, "end": v(24.25, -13.98) * mm});
            skLineSegment(sketch, "E51.trimOffspring", {"start": v(15.18, -6.07) * mm, "end": v(15.18, -13.98) * mm});
            skLineSegment(sketch, "E52.trimOffspring", {"start": v(21.08, 3.75) * mm, "end": v(24.25, 3.75) * mm});
            skPoint(sketch, "E53.0.1.0", {"position": v(19.72, 20.28) * mm});
            skLineSegment(sketch, "E53.0.1.1", {"start": v(21.08, 29.15) * mm, "end": v(24.25, 29.15) * mm});
            skLineSegment(sketch, "E53.0.1.2", {"start": v(24.25, 19.33) * mm, "end": v(24.25, 11.42) * mm});
            skLineSegment(sketch, "E53.0.1.3", {"start": v(20.84, 11.42) * mm, "end": v(24.25, 11.42) * mm});
            skLineSegment(sketch, "E53.0.1.4", {"start": v(13.9, 10.15) * mm, "end": v(25.52, 10.15) * mm});
            skLineSegment(sketch, "E53.0.1.5", {"start": v(13.9, 30.42) * mm, "end": v(13.9, 10.15) * mm});
            skLineSegment(sketch, "E53.0.1.6", {"start": v(24.25, 21.24) * mm, "end": v(20.97, 21.24) * mm});
            skLineSegment(sketch, "E53.0.1.7", {"start": v(24.25, 19.33) * mm, "end": v(20.95, 19.33) * mm});
            skLineSegment(sketch, "E53.0.1.8", {"start": v(18.6, 29.15) * mm, "end": v(18.49, 21.24) * mm});
            skLineSegment(sketch, "E53.0.1.9", {"start": v(21.08, 29.15) * mm, "end": v(20.97, 21.24) * mm});
            skLineSegment(sketch, "E53.0.1.10", {"start": v(24.25, 29.15) * mm, "end": v(24.25, 21.24) * mm});
            skLineSegment(sketch, "E53.0.1.11", {"start": v(15.18, 29.15) * mm, "end": v(15.18, 21.24) * mm});
            skLineSegment(sketch, "E53.0.1.12", {"start": v(15.18, 11.42) * mm, "end": v(18.35, 11.42) * mm});
            skLineSegment(sketch, "E53.0.1.13", {"start": v(15.18, 29.15) * mm, "end": v(18.6, 29.15) * mm});
            skLineSegment(sketch, "E53.0.1.14", {"start": v(20.95, 19.33) * mm, "end": v(20.84, 11.42) * mm});
            skLineSegment(sketch, "E53.0.1.15", {"start": v(18.46, 19.33) * mm, "end": v(15.18, 19.33) * mm});
            skLineSegment(sketch, "E53.0.1.16", {"start": v(18.46, 19.33) * mm, "end": v(18.35, 11.42) * mm});
            skLineSegment(sketch, "E53.0.1.17", {"start": v(13.9, 30.42) * mm, "end": v(25.52, 30.42) * mm});
            skLineSegment(sketch, "E53.0.1.18", {"start": v(25.52, 30.42) * mm, "end": v(25.52, 10.15) * mm});
            skLineSegment(sketch, "E53.0.1.19", {"start": v(18.49, 21.24) * mm, "end": v(15.18, 21.24) * mm});
            skPoint(sketch, "E53.0.1.20", {"position": v(24.25, 20.28) * mm});
            skPoint(sketch, "E53.0.1.21", {"position": v(19.72, 11.42) * mm});
            skLineSegment(sketch, "E53.0.1.22", {"start": v(15.18, 19.33) * mm, "end": v(15.18, 11.42) * mm});
            skPoint(sketch, "E53.0.1.23", {"position": v(19.72, 20.28) * mm});
            skPoint(sketch, "E53.0.1.24", {"position": v(19.72, 20.28) * mm});
            skPoint(sketch, "E53.0.2.0", {"position": v(19.72, 45.68) * mm});
            skLineSegment(sketch, "E53.0.2.1", {"start": v(21.08, 54.55) * mm, "end": v(24.25, 54.55) * mm});
            skLineSegment(sketch, "E53.0.2.2", {"start": v(24.25, 44.73) * mm, "end": v(24.25, 36.82) * mm});
            skLineSegment(sketch, "E53.0.2.3", {"start": v(20.84, 36.82) * mm, "end": v(24.25, 36.82) * mm});
            skLineSegment(sketch, "E53.0.2.4", {"start": v(13.9, 35.55) * mm, "end": v(25.52, 35.55) * mm});
            skLineSegment(sketch, "E53.0.2.5", {"start": v(13.9, 55.82) * mm, "end": v(13.9, 35.55) * mm});
            skLineSegment(sketch, "E53.0.2.6", {"start": v(24.25, 46.64) * mm, "end": v(20.97, 46.64) * mm});
            skLineSegment(sketch, "E53.0.2.7", {"start": v(24.25, 44.73) * mm, "end": v(20.95, 44.73) * mm});
            skLineSegment(sketch, "E53.0.2.8", {"start": v(18.6, 54.55) * mm, "end": v(18.49, 46.64) * mm});
            skLineSegment(sketch, "E53.0.2.9", {"start": v(21.08, 54.55) * mm, "end": v(20.97, 46.64) * mm});
            skLineSegment(sketch, "E53.0.2.10", {"start": v(24.25, 54.55) * mm, "end": v(24.25, 46.64) * mm});
            skLineSegment(sketch, "E53.0.2.11", {"start": v(15.18, 54.55) * mm, "end": v(15.18, 46.64) * mm});
            skLineSegment(sketch, "E53.0.2.12", {"start": v(15.18, 36.82) * mm, "end": v(18.35, 36.82) * mm});
            skLineSegment(sketch, "E53.0.2.13", {"start": v(15.18, 54.55) * mm, "end": v(18.6, 54.55) * mm});
            skLineSegment(sketch, "E53.0.2.14", {"start": v(20.95, 44.73) * mm, "end": v(20.84, 36.82) * mm});
            skLineSegment(sketch, "E53.0.2.15", {"start": v(18.46, 44.73) * mm, "end": v(15.18, 44.73) * mm});
            skLineSegment(sketch, "E53.0.2.16", {"start": v(18.46, 44.73) * mm, "end": v(18.35, 36.82) * mm});
            skLineSegment(sketch, "E53.0.2.17", {"start": v(13.9, 55.82) * mm, "end": v(25.52, 55.82) * mm});
            skLineSegment(sketch, "E53.0.2.18", {"start": v(25.52, 55.82) * mm, "end": v(25.52, 35.55) * mm});
            skLineSegment(sketch, "E53.0.2.19", {"start": v(18.49, 46.64) * mm, "end": v(15.18, 46.64) * mm});
            skPoint(sketch, "E53.0.2.20", {"position": v(24.25, 45.68) * mm});
            skPoint(sketch, "E53.0.2.21", {"position": v(19.72, 36.82) * mm});
            skLineSegment(sketch, "E53.0.2.22", {"start": v(15.18, 44.73) * mm, "end": v(15.18, 36.82) * mm});
            skPoint(sketch, "E53.0.2.23", {"position": v(19.72, 45.68) * mm});
            skPoint(sketch, "E53.0.2.24", {"position": v(19.72, 45.68) * mm});
            skPoint(sketch, "E53.0.3.0", {"position": v(19.72, 71.08) * mm});
            skLineSegment(sketch, "E53.0.3.1", {"start": v(21.08, 79.95) * mm, "end": v(24.25, 79.95) * mm});
            skLineSegment(sketch, "E53.0.3.2", {"start": v(24.25, 70.13) * mm, "end": v(24.25, 62.22) * mm});
            skLineSegment(sketch, "E53.0.3.3", {"start": v(20.84, 62.22) * mm, "end": v(24.25, 62.22) * mm});
            skLineSegment(sketch, "E53.0.3.4", {"start": v(13.9, 60.95) * mm, "end": v(25.52, 60.95) * mm});
            skLineSegment(sketch, "E53.0.3.5", {"start": v(13.9, 81.22) * mm, "end": v(13.9, 60.95) * mm});
            skLineSegment(sketch, "E53.0.3.6", {"start": v(24.25, 72.04) * mm, "end": v(20.97, 72.04) * mm});
            skLineSegment(sketch, "E53.0.3.7", {"start": v(24.25, 70.13) * mm, "end": v(20.95, 70.13) * mm});
            skLineSegment(sketch, "E53.0.3.8", {"start": v(18.6, 79.95) * mm, "end": v(18.49, 72.04) * mm});
            skLineSegment(sketch, "E53.0.3.9", {"start": v(21.08, 79.95) * mm, "end": v(20.97, 72.04) * mm});
            skLineSegment(sketch, "E53.0.3.10", {"start": v(24.25, 79.95) * mm, "end": v(24.25, 72.04) * mm});
            skLineSegment(sketch, "E53.0.3.11", {"start": v(15.18, 79.95) * mm, "end": v(15.18, 72.04) * mm});
            skLineSegment(sketch, "E53.0.3.12", {"start": v(15.18, 62.22) * mm, "end": v(18.35, 62.22) * mm});
            skLineSegment(sketch, "E53.0.3.13", {"start": v(15.18, 79.95) * mm, "end": v(18.6, 79.95) * mm});
            skLineSegment(sketch, "E53.0.3.14", {"start": v(20.95, 70.13) * mm, "end": v(20.84, 62.22) * mm});
            skLineSegment(sketch, "E53.0.3.15", {"start": v(18.46, 70.13) * mm, "end": v(15.18, 70.13) * mm});
            skLineSegment(sketch, "E53.0.3.16", {"start": v(18.46, 70.13) * mm, "end": v(18.35, 62.22) * mm});
            skLineSegment(sketch, "E53.0.3.17", {"start": v(13.9, 81.22) * mm, "end": v(25.52, 81.22) * mm});
            skLineSegment(sketch, "E53.0.3.18", {"start": v(25.52, 81.22) * mm, "end": v(25.52, 60.95) * mm});
            skLineSegment(sketch, "E53.0.3.19", {"start": v(18.49, 72.04) * mm, "end": v(15.18, 72.04) * mm});
            skPoint(sketch, "E53.0.3.20", {"position": v(24.25, 71.08) * mm});
            skPoint(sketch, "E53.0.3.21", {"position": v(19.72, 62.22) * mm});
            skLineSegment(sketch, "E53.0.3.22", {"start": v(15.18, 70.13) * mm, "end": v(15.18, 62.22) * mm});
            skPoint(sketch, "E53.0.3.23", {"position": v(19.72, 71.08) * mm});
            skPoint(sketch, "E53.0.3.24", {"position": v(19.72, 71.08) * mm});
            skPoint(sketch, "E53.1.0.0", {"position": v(44.6, -5.12) * mm});
            skLineSegment(sketch, "E53.1.0.1", {"start": v(45.98, 3.75) * mm, "end": v(49.15, 3.75) * mm});
            skLineSegment(sketch, "E53.1.0.2", {"start": v(49.15, -6.07) * mm, "end": v(49.15, -13.98) * mm});
            skLineSegment(sketch, "E53.1.0.3", {"start": v(45.73, -13.98) * mm, "end": v(49.15, -13.98) * mm});
            skLineSegment(sketch, "E53.1.0.4", {"start": v(38.8, -15.25) * mm, "end": v(50.42, -15.25) * mm});
            skLineSegment(sketch, "E53.1.0.5", {"start": v(38.8, 5.02) * mm, "end": v(38.8, -15.25) * mm});
            skLineSegment(sketch, "E53.1.0.6", {"start": v(49.15, -4.16) * mm, "end": v(45.87, -4.16) * mm});
            skLineSegment(sketch, "E53.1.0.7", {"start": v(49.15, -6.07) * mm, "end": v(45.84, -6.07) * mm});
            skLineSegment(sketch, "E53.1.0.8", {"start": v(43.49, 3.75) * mm, "end": v(43.38, -4.16) * mm});
            skLineSegment(sketch, "E53.1.0.9", {"start": v(45.98, 3.75) * mm, "end": v(45.87, -4.16) * mm});
            skLineSegment(sketch, "E53.1.0.10", {"start": v(49.15, 3.75) * mm, "end": v(49.15, -4.16) * mm});
            skLineSegment(sketch, "E53.1.0.11", {"start": v(40.07, 3.75) * mm, "end": v(40.07, -4.16) * mm});
            skLineSegment(sketch, "E53.1.0.12", {"start": v(40.07, -13.98) * mm, "end": v(43.24, -13.98) * mm});
            skLineSegment(sketch, "E53.1.0.13", {"start": v(40.07, 3.75) * mm, "end": v(43.49, 3.75) * mm});
            skLineSegment(sketch, "E53.1.0.14", {"start": v(45.84, -6.07) * mm, "end": v(45.73, -13.98) * mm});
            skLineSegment(sketch, "E53.1.0.15", {"start": v(43.35, -6.07) * mm, "end": v(40.07, -6.07) * mm});
            skLineSegment(sketch, "E53.1.0.16", {"start": v(43.35, -6.07) * mm, "end": v(43.24, -13.98) * mm});
            skLineSegment(sketch, "E53.1.0.17", {"start": v(38.8, 5.02) * mm, "end": v(50.42, 5.02) * mm});
            skLineSegment(sketch, "E53.1.0.18", {"start": v(50.42, 5.02) * mm, "end": v(50.42, -15.25) * mm});
            skLineSegment(sketch, "E53.1.0.19", {"start": v(43.38, -4.16) * mm, "end": v(40.07, -4.16) * mm});
            skPoint(sketch, "E53.1.0.20", {"position": v(49.15, -5.12) * mm});
            skPoint(sketch, "E53.1.0.21", {"position": v(44.6, -13.98) * mm});
            skLineSegment(sketch, "E53.1.0.22", {"start": v(40.07, -6.07) * mm, "end": v(40.07, -13.98) * mm});
            skPoint(sketch, "E53.1.0.23", {"position": v(44.6, -5.12) * mm});
            skPoint(sketch, "E53.1.0.24", {"position": v(44.6, -5.12) * mm});
            skPoint(sketch, "E53.1.1.0", {"position": v(44.6, 20.28) * mm});
            skLineSegment(sketch, "E53.1.1.1", {"start": v(45.98, 29.15) * mm, "end": v(49.15, 29.15) * mm});
            skLineSegment(sketch, "E53.1.1.2", {"start": v(49.15, 19.33) * mm, "end": v(49.15, 11.42) * mm});
            skLineSegment(sketch, "E53.1.1.3", {"start": v(45.73, 11.42) * mm, "end": v(49.15, 11.42) * mm});
            skLineSegment(sketch, "E53.1.1.4", {"start": v(38.8, 10.15) * mm, "end": v(50.42, 10.15) * mm});
            skLineSegment(sketch, "E53.1.1.5", {"start": v(38.8, 30.42) * mm, "end": v(38.8, 10.15) * mm});
            skLineSegment(sketch, "E53.1.1.6", {"start": v(49.15, 21.24) * mm, "end": v(45.87, 21.24) * mm});
            skLineSegment(sketch, "E53.1.1.7", {"start": v(49.15, 19.33) * mm, "end": v(45.84, 19.33) * mm});
            skLineSegment(sketch, "E53.1.1.8", {"start": v(43.49, 29.15) * mm, "end": v(43.38, 21.24) * mm});
            skLineSegment(sketch, "E53.1.1.9", {"start": v(45.98, 29.15) * mm, "end": v(45.87, 21.24) * mm});
            skLineSegment(sketch, "E53.1.1.10", {"start": v(49.15, 29.15) * mm, "end": v(49.15, 21.24) * mm});
            skLineSegment(sketch, "E53.1.1.11", {"start": v(40.07, 29.15) * mm, "end": v(40.07, 21.24) * mm});
            skLineSegment(sketch, "E53.1.1.12", {"start": v(40.07, 11.42) * mm, "end": v(43.24, 11.42) * mm});
            skLineSegment(sketch, "E53.1.1.13", {"start": v(40.07, 29.15) * mm, "end": v(43.49, 29.15) * mm});
            skLineSegment(sketch, "E53.1.1.14", {"start": v(45.84, 19.33) * mm, "end": v(45.73, 11.42) * mm});
            skLineSegment(sketch, "E53.1.1.15", {"start": v(43.35, 19.33) * mm, "end": v(40.07, 19.33) * mm});
            skLineSegment(sketch, "E53.1.1.16", {"start": v(43.35, 19.33) * mm, "end": v(43.24, 11.42) * mm});
            skLineSegment(sketch, "E53.1.1.17", {"start": v(38.8, 30.42) * mm, "end": v(50.42, 30.42) * mm});
            skLineSegment(sketch, "E53.1.1.18", {"start": v(50.42, 30.42) * mm, "end": v(50.42, 10.15) * mm});
            skLineSegment(sketch, "E53.1.1.19", {"start": v(43.38, 21.24) * mm, "end": v(40.07, 21.24) * mm});
            skPoint(sketch, "E53.1.1.20", {"position": v(49.15, 20.28) * mm});
            skPoint(sketch, "E53.1.1.21", {"position": v(44.6, 11.42) * mm});
            skLineSegment(sketch, "E53.1.1.22", {"start": v(40.07, 19.33) * mm, "end": v(40.07, 11.42) * mm});
            skPoint(sketch, "E53.1.1.23", {"position": v(44.6, 20.28) * mm});
            skPoint(sketch, "E53.1.1.24", {"position": v(44.6, 20.28) * mm});
            skPoint(sketch, "E53.1.2.0", {"position": v(44.6, 45.68) * mm});
            skLineSegment(sketch, "E53.1.2.1", {"start": v(45.98, 54.55) * mm, "end": v(49.15, 54.55) * mm});
            skLineSegment(sketch, "E53.1.2.2", {"start": v(49.15, 44.73) * mm, "end": v(49.15, 36.82) * mm});
            skLineSegment(sketch, "E53.1.2.3", {"start": v(45.73, 36.82) * mm, "end": v(49.15, 36.82) * mm});
            skLineSegment(sketch, "E53.1.2.4", {"start": v(38.8, 35.55) * mm, "end": v(50.42, 35.55) * mm});
            skLineSegment(sketch, "E53.1.2.5", {"start": v(38.8, 55.82) * mm, "end": v(38.8, 35.55) * mm});
            skLineSegment(sketch, "E53.1.2.6", {"start": v(49.15, 46.64) * mm, "end": v(45.87, 46.64) * mm});
            skLineSegment(sketch, "E53.1.2.7", {"start": v(49.15, 44.73) * mm, "end": v(45.84, 44.73) * mm});
            skLineSegment(sketch, "E53.1.2.8", {"start": v(43.49, 54.55) * mm, "end": v(43.38, 46.64) * mm});
            skLineSegment(sketch, "E53.1.2.9", {"start": v(45.98, 54.55) * mm, "end": v(45.87, 46.64) * mm});
            skLineSegment(sketch, "E53.1.2.10", {"start": v(49.15, 54.55) * mm, "end": v(49.15, 46.64) * mm});
            skLineSegment(sketch, "E53.1.2.11", {"start": v(40.07, 54.55) * mm, "end": v(40.07, 46.64) * mm});
            skLineSegment(sketch, "E53.1.2.12", {"start": v(40.07, 36.82) * mm, "end": v(43.24, 36.82) * mm});
            skLineSegment(sketch, "E53.1.2.13", {"start": v(40.07, 54.55) * mm, "end": v(43.49, 54.55) * mm});
            skLineSegment(sketch, "E53.1.2.14", {"start": v(45.84, 44.73) * mm, "end": v(45.73, 36.82) * mm});
            skLineSegment(sketch, "E53.1.2.15", {"start": v(43.35, 44.73) * mm, "end": v(40.07, 44.73) * mm});
            skLineSegment(sketch, "E53.1.2.16", {"start": v(43.35, 44.73) * mm, "end": v(43.24, 36.82) * mm});
            skLineSegment(sketch, "E53.1.2.17", {"start": v(38.8, 55.82) * mm, "end": v(50.42, 55.82) * mm});
            skLineSegment(sketch, "E53.1.2.18", {"start": v(50.42, 55.82) * mm, "end": v(50.42, 35.55) * mm});
            skLineSegment(sketch, "E53.1.2.19", {"start": v(43.38, 46.64) * mm, "end": v(40.07, 46.64) * mm});
            skPoint(sketch, "E53.1.2.20", {"position": v(49.15, 45.68) * mm});
            skPoint(sketch, "E53.1.2.21", {"position": v(44.6, 36.82) * mm});
            skLineSegment(sketch, "E53.1.2.22", {"start": v(40.07, 44.73) * mm, "end": v(40.07, 36.82) * mm});
            skPoint(sketch, "E53.1.2.23", {"position": v(44.6, 45.68) * mm});
            skPoint(sketch, "E53.1.2.24", {"position": v(44.6, 45.68) * mm});
            skPoint(sketch, "E53.1.3.0", {"position": v(44.6, 71.08) * mm});
            skLineSegment(sketch, "E53.1.3.1", {"start": v(45.98, 79.95) * mm, "end": v(49.15, 79.95) * mm});
            skLineSegment(sketch, "E53.1.3.2", {"start": v(49.15, 70.13) * mm, "end": v(49.15, 62.22) * mm});
            skLineSegment(sketch, "E53.1.3.3", {"start": v(45.73, 62.22) * mm, "end": v(49.15, 62.22) * mm});
            skLineSegment(sketch, "E53.1.3.4", {"start": v(38.8, 60.95) * mm, "end": v(50.42, 60.95) * mm});
            skLineSegment(sketch, "E53.1.3.5", {"start": v(38.8, 81.22) * mm, "end": v(38.8, 60.95) * mm});
            skLineSegment(sketch, "E53.1.3.6", {"start": v(49.15, 72.04) * mm, "end": v(45.87, 72.04) * mm});
            skLineSegment(sketch, "E53.1.3.7", {"start": v(49.15, 70.13) * mm, "end": v(45.84, 70.13) * mm});
            skLineSegment(sketch, "E53.1.3.8", {"start": v(43.49, 79.95) * mm, "end": v(43.38, 72.04) * mm});
            skLineSegment(sketch, "E53.1.3.9", {"start": v(45.98, 79.95) * mm, "end": v(45.87, 72.04) * mm});
            skLineSegment(sketch, "E53.1.3.10", {"start": v(49.15, 79.95) * mm, "end": v(49.15, 72.04) * mm});
            skLineSegment(sketch, "E53.1.3.11", {"start": v(40.07, 79.95) * mm, "end": v(40.07, 72.04) * mm});
            skLineSegment(sketch, "E53.1.3.12", {"start": v(40.07, 62.22) * mm, "end": v(43.24, 62.22) * mm});
            skLineSegment(sketch, "E53.1.3.13", {"start": v(40.07, 79.95) * mm, "end": v(43.49, 79.95) * mm});
            skLineSegment(sketch, "E53.1.3.14", {"start": v(45.84, 70.13) * mm, "end": v(45.73, 62.22) * mm});
            skLineSegment(sketch, "E53.1.3.15", {"start": v(43.35, 70.13) * mm, "end": v(40.07, 70.13) * mm});
            skLineSegment(sketch, "E53.1.3.16", {"start": v(43.35, 70.13) * mm, "end": v(43.24, 62.22) * mm});
            skLineSegment(sketch, "E53.1.3.17", {"start": v(38.8, 81.22) * mm, "end": v(50.42, 81.22) * mm});
            skLineSegment(sketch, "E53.1.3.18", {"start": v(50.42, 81.22) * mm, "end": v(50.42, 60.95) * mm});
            skLineSegment(sketch, "E53.1.3.19", {"start": v(43.38, 72.04) * mm, "end": v(40.07, 72.04) * mm});
            skPoint(sketch, "E53.1.3.20", {"position": v(49.15, 71.08) * mm});
            skPoint(sketch, "E53.1.3.21", {"position": v(44.6, 62.22) * mm});
            skLineSegment(sketch, "E53.1.3.22", {"start": v(40.07, 70.13) * mm, "end": v(40.07, 62.22) * mm});
            skPoint(sketch, "E53.1.3.23", {"position": v(44.6, 71.08) * mm});
            skPoint(sketch, "E53.1.3.24", {"position": v(44.6, 71.08) * mm});
            skPoint(sketch, "E53.2.0.0", {"position": v(69.5, -5.12) * mm});
            skLineSegment(sketch, "E53.2.0.1", {"start": v(70.87, 3.75) * mm, "end": v(74.04, 3.75) * mm});
            skLineSegment(sketch, "E53.2.0.2", {"start": v(74.04, -6.07) * mm, "end": v(74.04, -13.98) * mm});
            skLineSegment(sketch, "E53.2.0.3", {"start": v(70.62, -13.98) * mm, "end": v(74.04, -13.98) * mm});
            skLineSegment(sketch, "E53.2.0.4", {"start": v(63.7, -15.25) * mm, "end": v(75.3, -15.25) * mm});
            skLineSegment(sketch, "E53.2.0.5", {"start": v(63.7, 5.02) * mm, "end": v(63.7, -15.25) * mm});
            skLineSegment(sketch, "E53.2.0.6", {"start": v(74.04, -4.16) * mm, "end": v(70.76, -4.16) * mm});
            skLineSegment(sketch, "E53.2.0.7", {"start": v(74.04, -6.07) * mm, "end": v(70.73, -6.07) * mm});
            skLineSegment(sketch, "E53.2.0.8", {"start": v(68.38, 3.75) * mm, "end": v(68.27, -4.16) * mm});
            skLineSegment(sketch, "E53.2.0.9", {"start": v(70.87, 3.75) * mm, "end": v(70.76, -4.16) * mm});
            skLineSegment(sketch, "E53.2.0.10", {"start": v(74.04, 3.75) * mm, "end": v(74.04, -4.16) * mm});
            skLineSegment(sketch, "E53.2.0.11", {"start": v(64.96, 3.75) * mm, "end": v(64.96, -4.16) * mm});
            skLineSegment(sketch, "E53.2.0.12", {"start": v(64.96, -13.98) * mm, "end": v(68.13, -13.98) * mm});
            skLineSegment(sketch, "E53.2.0.13", {"start": v(64.96, 3.75) * mm, "end": v(68.38, 3.75) * mm});
            skLineSegment(sketch, "E53.2.0.14", {"start": v(70.73, -6.07) * mm, "end": v(70.62, -13.98) * mm});
            skLineSegment(sketch, "E53.2.0.15", {"start": v(68.24, -6.07) * mm, "end": v(64.96, -6.07) * mm});
            skLineSegment(sketch, "E53.2.0.16", {"start": v(68.24, -6.07) * mm, "end": v(68.13, -13.98) * mm});
            skLineSegment(sketch, "E53.2.0.17", {"start": v(63.7, 5.02) * mm, "end": v(75.3, 5.02) * mm});
            skLineSegment(sketch, "E53.2.0.18", {"start": v(75.3, 5.02) * mm, "end": v(75.3, -15.25) * mm});
            skLineSegment(sketch, "E53.2.0.19", {"start": v(68.27, -4.16) * mm, "end": v(64.96, -4.16) * mm});
            skPoint(sketch, "E53.2.0.20", {"position": v(74.04, -5.12) * mm});
            skPoint(sketch, "E53.2.0.21", {"position": v(69.5, -13.98) * mm});
            skLineSegment(sketch, "E53.2.0.22", {"start": v(64.96, -6.07) * mm, "end": v(64.96, -13.98) * mm});
            skPoint(sketch, "E53.2.0.23", {"position": v(69.5, -5.12) * mm});
            skPoint(sketch, "E53.2.0.24", {"position": v(69.5, -5.12) * mm});
            skPoint(sketch, "E53.2.1.0", {"position": v(69.5, 20.28) * mm});
            skLineSegment(sketch, "E53.2.1.1", {"start": v(70.87, 29.15) * mm, "end": v(74.04, 29.15) * mm});
            skLineSegment(sketch, "E53.2.1.2", {"start": v(74.04, 19.33) * mm, "end": v(74.04, 11.42) * mm});
            skLineSegment(sketch, "E53.2.1.3", {"start": v(70.62, 11.42) * mm, "end": v(74.04, 11.42) * mm});
            skLineSegment(sketch, "E53.2.1.4", {"start": v(63.7, 10.15) * mm, "end": v(75.3, 10.15) * mm});
            skLineSegment(sketch, "E53.2.1.5", {"start": v(63.7, 30.42) * mm, "end": v(63.7, 10.15) * mm});
            skLineSegment(sketch, "E53.2.1.6", {"start": v(74.04, 21.24) * mm, "end": v(70.76, 21.24) * mm});
            skLineSegment(sketch, "E53.2.1.7", {"start": v(74.04, 19.33) * mm, "end": v(70.73, 19.33) * mm});
            skLineSegment(sketch, "E53.2.1.8", {"start": v(68.38, 29.15) * mm, "end": v(68.27, 21.24) * mm});
            skLineSegment(sketch, "E53.2.1.9", {"start": v(70.87, 29.15) * mm, "end": v(70.76, 21.24) * mm});
            skLineSegment(sketch, "E53.2.1.10", {"start": v(74.04, 29.15) * mm, "end": v(74.04, 21.24) * mm});
            skLineSegment(sketch, "E53.2.1.11", {"start": v(64.96, 29.15) * mm, "end": v(64.96, 21.24) * mm});
            skLineSegment(sketch, "E53.2.1.12", {"start": v(64.96, 11.42) * mm, "end": v(68.13, 11.42) * mm});
            skLineSegment(sketch, "E53.2.1.13", {"start": v(64.96, 29.15) * mm, "end": v(68.38, 29.15) * mm});
            skLineSegment(sketch, "E53.2.1.14", {"start": v(70.73, 19.33) * mm, "end": v(70.62, 11.42) * mm});
            skLineSegment(sketch, "E53.2.1.15", {"start": v(68.24, 19.33) * mm, "end": v(64.96, 19.33) * mm});
            skLineSegment(sketch, "E53.2.1.16", {"start": v(68.24, 19.33) * mm, "end": v(68.13, 11.42) * mm});
            skLineSegment(sketch, "E53.2.1.17", {"start": v(63.7, 30.42) * mm, "end": v(75.3, 30.42) * mm});
            skLineSegment(sketch, "E53.2.1.18", {"start": v(75.3, 30.42) * mm, "end": v(75.3, 10.15) * mm});
            skLineSegment(sketch, "E53.2.1.19", {"start": v(68.27, 21.24) * mm, "end": v(64.96, 21.24) * mm});
            skPoint(sketch, "E53.2.1.20", {"position": v(74.04, 20.28) * mm});
            skPoint(sketch, "E53.2.1.21", {"position": v(69.5, 11.42) * mm});
            skLineSegment(sketch, "E53.2.1.22", {"start": v(64.96, 19.33) * mm, "end": v(64.96, 11.42) * mm});
            skPoint(sketch, "E53.2.1.23", {"position": v(69.5, 20.28) * mm});
            skPoint(sketch, "E53.2.1.24", {"position": v(69.5, 20.28) * mm});
            skPoint(sketch, "E53.2.2.0", {"position": v(69.5, 45.68) * mm});
            skLineSegment(sketch, "E53.2.2.1", {"start": v(70.87, 54.55) * mm, "end": v(74.04, 54.55) * mm});
            skLineSegment(sketch, "E53.2.2.2", {"start": v(74.04, 44.73) * mm, "end": v(74.04, 36.82) * mm});
            skLineSegment(sketch, "E53.2.2.3", {"start": v(70.62, 36.82) * mm, "end": v(74.04, 36.82) * mm});
            skLineSegment(sketch, "E53.2.2.4", {"start": v(63.7, 35.55) * mm, "end": v(75.3, 35.55) * mm});
            skLineSegment(sketch, "E53.2.2.5", {"start": v(63.7, 55.82) * mm, "end": v(63.7, 35.55) * mm});
            skLineSegment(sketch, "E53.2.2.6", {"start": v(74.04, 46.64) * mm, "end": v(70.76, 46.64) * mm});
            skLineSegment(sketch, "E53.2.2.7", {"start": v(74.04, 44.73) * mm, "end": v(70.73, 44.73) * mm});
            skLineSegment(sketch, "E53.2.2.8", {"start": v(68.38, 54.55) * mm, "end": v(68.27, 46.64) * mm});
            skLineSegment(sketch, "E53.2.2.9", {"start": v(70.87, 54.55) * mm, "end": v(70.76, 46.64) * mm});
            skLineSegment(sketch, "E53.2.2.10", {"start": v(74.04, 54.55) * mm, "end": v(74.04, 46.64) * mm});
            skLineSegment(sketch, "E53.2.2.11", {"start": v(64.96, 54.55) * mm, "end": v(64.96, 46.64) * mm});
            skLineSegment(sketch, "E53.2.2.12", {"start": v(64.96, 36.82) * mm, "end": v(68.13, 36.82) * mm});
            skLineSegment(sketch, "E53.2.2.13", {"start": v(64.96, 54.55) * mm, "end": v(68.38, 54.55) * mm});
            skLineSegment(sketch, "E53.2.2.14", {"start": v(70.73, 44.73) * mm, "end": v(70.62, 36.82) * mm});
            skLineSegment(sketch, "E53.2.2.15", {"start": v(68.24, 44.73) * mm, "end": v(64.96, 44.73) * mm});
            skLineSegment(sketch, "E53.2.2.16", {"start": v(68.24, 44.73) * mm, "end": v(68.13, 36.82) * mm});
            skLineSegment(sketch, "E53.2.2.17", {"start": v(63.7, 55.82) * mm, "end": v(75.3, 55.82) * mm});
            skLineSegment(sketch, "E53.2.2.18", {"start": v(75.3, 55.82) * mm, "end": v(75.3, 35.55) * mm});
            skLineSegment(sketch, "E53.2.2.19", {"start": v(68.27, 46.64) * mm, "end": v(64.96, 46.64) * mm});
            skPoint(sketch, "E53.2.2.20", {"position": v(74.04, 45.68) * mm});
            skPoint(sketch, "E53.2.2.21", {"position": v(69.5, 36.82) * mm});
            skLineSegment(sketch, "E53.2.2.22", {"start": v(64.96, 44.73) * mm, "end": v(64.96, 36.82) * mm});
            skPoint(sketch, "E53.2.2.23", {"position": v(69.5, 45.68) * mm});
            skPoint(sketch, "E53.2.2.24", {"position": v(69.5, 45.68) * mm});
            skPoint(sketch, "E53.2.3.0", {"position": v(69.5, 71.08) * mm});
            skLineSegment(sketch, "E53.2.3.1", {"start": v(70.87, 79.95) * mm, "end": v(74.04, 79.95) * mm});
            skLineSegment(sketch, "E53.2.3.2", {"start": v(74.04, 70.13) * mm, "end": v(74.04, 62.22) * mm});
            skLineSegment(sketch, "E53.2.3.3", {"start": v(70.62, 62.22) * mm, "end": v(74.04, 62.22) * mm});
            skLineSegment(sketch, "E53.2.3.4", {"start": v(63.7, 60.95) * mm, "end": v(75.3, 60.95) * mm});
            skLineSegment(sketch, "E53.2.3.5", {"start": v(63.7, 81.22) * mm, "end": v(63.7, 60.95) * mm});
            skLineSegment(sketch, "E53.2.3.6", {"start": v(74.04, 72.04) * mm, "end": v(70.76, 72.04) * mm});
            skLineSegment(sketch, "E53.2.3.7", {"start": v(74.04, 70.13) * mm, "end": v(70.73, 70.13) * mm});
            skLineSegment(sketch, "E53.2.3.8", {"start": v(68.38, 79.95) * mm, "end": v(68.27, 72.04) * mm});
            skLineSegment(sketch, "E53.2.3.9", {"start": v(70.87, 79.95) * mm, "end": v(70.76, 72.04) * mm});
            skLineSegment(sketch, "E53.2.3.10", {"start": v(74.04, 79.95) * mm, "end": v(74.04, 72.04) * mm});
            skLineSegment(sketch, "E53.2.3.11", {"start": v(64.96, 79.95) * mm, "end": v(64.96, 72.04) * mm});
            skLineSegment(sketch, "E53.2.3.12", {"start": v(64.96, 62.22) * mm, "end": v(68.13, 62.22) * mm});
            skLineSegment(sketch, "E53.2.3.13", {"start": v(64.96, 79.95) * mm, "end": v(68.38, 79.95) * mm});
            skLineSegment(sketch, "E53.2.3.14", {"start": v(70.73, 70.13) * mm, "end": v(70.62, 62.22) * mm});
            skLineSegment(sketch, "E53.2.3.15", {"start": v(68.24, 70.13) * mm, "end": v(64.96, 70.13) * mm});
            skLineSegment(sketch, "E53.2.3.16", {"start": v(68.24, 70.13) * mm, "end": v(68.13, 62.22) * mm});
            skLineSegment(sketch, "E53.2.3.17", {"start": v(63.7, 81.22) * mm, "end": v(75.3, 81.22) * mm});
            skLineSegment(sketch, "E53.2.3.18", {"start": v(75.3, 81.22) * mm, "end": v(75.3, 60.95) * mm});
            skLineSegment(sketch, "E53.2.3.19", {"start": v(68.27, 72.04) * mm, "end": v(64.96, 72.04) * mm});
            skPoint(sketch, "E53.2.3.20", {"position": v(74.04, 71.08) * mm});
            skPoint(sketch, "E53.2.3.21", {"position": v(69.5, 62.22) * mm});
            skLineSegment(sketch, "E53.2.3.22", {"start": v(64.96, 70.13) * mm, "end": v(64.96, 62.22) * mm});
            skPoint(sketch, "E53.2.3.23", {"position": v(69.5, 71.08) * mm});
            skPoint(sketch, "E53.2.3.24", {"position": v(69.5, 71.08) * mm});
            skPoint(sketch, "E53.3.0.0", {"position": v(94.4, -5.12) * mm});
            skLineSegment(sketch, "E53.3.0.1", {"start": v(95.76, 3.75) * mm, "end": v(98.93, 3.75) * mm});
            skLineSegment(sketch, "E53.3.0.2", {"start": v(98.93, -6.07) * mm, "end": v(98.93, -13.98) * mm});
            skLineSegment(sketch, "E53.3.0.3", {"start": v(95.51, -13.98) * mm, "end": v(98.93, -13.98) * mm});
            skLineSegment(sketch, "E53.3.0.4", {"start": v(88.58, -15.25) * mm, "end": v(100.2, -15.25) * mm});
            skLineSegment(sketch, "E53.3.0.5", {"start": v(88.58, 5.02) * mm, "end": v(88.58, -15.25) * mm});
            skLineSegment(sketch, "E53.3.0.6", {"start": v(98.93, -4.16) * mm, "end": v(95.65, -4.16) * mm});
            skLineSegment(sketch, "E53.3.0.7", {"start": v(98.93, -6.07) * mm, "end": v(95.62, -6.07) * mm});
            skLineSegment(sketch, "E53.3.0.8", {"start": v(93.27, 3.75) * mm, "end": v(93.16, -4.16) * mm});
            skLineSegment(sketch, "E53.3.0.9", {"start": v(95.76, 3.75) * mm, "end": v(95.65, -4.16) * mm});
            skLineSegment(sketch, "E53.3.0.10", {"start": v(98.93, 3.75) * mm, "end": v(98.93, -4.16) * mm});
            skLineSegment(sketch, "E53.3.0.11", {"start": v(89.85, 3.75) * mm, "end": v(89.85, -4.16) * mm});
            skLineSegment(sketch, "E53.3.0.12", {"start": v(89.85, -13.98) * mm, "end": v(93.02, -13.98) * mm});
            skLineSegment(sketch, "E53.3.0.13", {"start": v(89.85, 3.75) * mm, "end": v(93.27, 3.75) * mm});
            skLineSegment(sketch, "E53.3.0.14", {"start": v(95.62, -6.07) * mm, "end": v(95.51, -13.98) * mm});
            skLineSegment(sketch, "E53.3.0.15", {"start": v(93.13, -6.07) * mm, "end": v(89.85, -6.07) * mm});
            skLineSegment(sketch, "E53.3.0.16", {"start": v(93.13, -6.07) * mm, "end": v(93.02, -13.98) * mm});
            skLineSegment(sketch, "E53.3.0.17", {"start": v(88.58, 5.02) * mm, "end": v(100.2, 5.02) * mm});
            skLineSegment(sketch, "E53.3.0.18", {"start": v(100.2, 5.02) * mm, "end": v(100.2, -15.25) * mm});
            skLineSegment(sketch, "E53.3.0.19", {"start": v(93.16, -4.16) * mm, "end": v(89.85, -4.16) * mm});
            skPoint(sketch, "E53.3.0.20", {"position": v(98.93, -5.12) * mm});
            skPoint(sketch, "E53.3.0.21", {"position": v(94.4, -13.98) * mm});
            skLineSegment(sketch, "E53.3.0.22", {"start": v(89.85, -6.07) * mm, "end": v(89.85, -13.98) * mm});
            skPoint(sketch, "E53.3.0.23", {"position": v(94.4, -5.12) * mm});
            skPoint(sketch, "E53.3.0.24", {"position": v(94.4, -5.12) * mm});
            skPoint(sketch, "E53.3.1.0", {"position": v(94.4, 20.28) * mm});
            skLineSegment(sketch, "E53.3.1.1", {"start": v(95.76, 29.15) * mm, "end": v(98.93, 29.15) * mm});
            skLineSegment(sketch, "E53.3.1.2", {"start": v(98.93, 19.33) * mm, "end": v(98.93, 11.42) * mm});
            skLineSegment(sketch, "E53.3.1.3", {"start": v(95.51, 11.42) * mm, "end": v(98.93, 11.42) * mm});
            skLineSegment(sketch, "E53.3.1.4", {"start": v(88.58, 10.15) * mm, "end": v(100.2, 10.15) * mm});
            skLineSegment(sketch, "E53.3.1.5", {"start": v(88.58, 30.42) * mm, "end": v(88.58, 10.15) * mm});
            skLineSegment(sketch, "E53.3.1.6", {"start": v(98.93, 21.24) * mm, "end": v(95.65, 21.24) * mm});
            skLineSegment(sketch, "E53.3.1.7", {"start": v(98.93, 19.33) * mm, "end": v(95.62, 19.33) * mm});
            skLineSegment(sketch, "E53.3.1.8", {"start": v(93.27, 29.15) * mm, "end": v(93.16, 21.24) * mm});
            skLineSegment(sketch, "E53.3.1.9", {"start": v(95.76, 29.15) * mm, "end": v(95.65, 21.24) * mm});
            skLineSegment(sketch, "E53.3.1.10", {"start": v(98.93, 29.15) * mm, "end": v(98.93, 21.24) * mm});
            skLineSegment(sketch, "E53.3.1.11", {"start": v(89.85, 29.15) * mm, "end": v(89.85, 21.24) * mm});
            skLineSegment(sketch, "E53.3.1.12", {"start": v(89.85, 11.42) * mm, "end": v(93.02, 11.42) * mm});
            skLineSegment(sketch, "E53.3.1.13", {"start": v(89.85, 29.15) * mm, "end": v(93.27, 29.15) * mm});
            skLineSegment(sketch, "E53.3.1.14", {"start": v(95.62, 19.33) * mm, "end": v(95.51, 11.42) * mm});
            skLineSegment(sketch, "E53.3.1.15", {"start": v(93.13, 19.33) * mm, "end": v(89.85, 19.33) * mm});
            skLineSegment(sketch, "E53.3.1.16", {"start": v(93.13, 19.33) * mm, "end": v(93.02, 11.42) * mm});
            skLineSegment(sketch, "E53.3.1.17", {"start": v(88.58, 30.42) * mm, "end": v(100.2, 30.42) * mm});
            skLineSegment(sketch, "E53.3.1.18", {"start": v(100.2, 30.42) * mm, "end": v(100.2, 10.15) * mm});
            skLineSegment(sketch, "E53.3.1.19", {"start": v(93.16, 21.24) * mm, "end": v(89.85, 21.24) * mm});
            skPoint(sketch, "E53.3.1.20", {"position": v(98.93, 20.28) * mm});
            skPoint(sketch, "E53.3.1.21", {"position": v(94.4, 11.42) * mm});
            skLineSegment(sketch, "E53.3.1.22", {"start": v(89.85, 19.33) * mm, "end": v(89.85, 11.42) * mm});
            skPoint(sketch, "E53.3.1.23", {"position": v(94.4, 20.28) * mm});
            skPoint(sketch, "E53.3.1.24", {"position": v(94.4, 20.28) * mm});
            skPoint(sketch, "E53.3.2.0", {"position": v(94.4, 45.68) * mm});
            skLineSegment(sketch, "E53.3.2.1", {"start": v(95.76, 54.55) * mm, "end": v(98.93, 54.55) * mm});
            skLineSegment(sketch, "E53.3.2.2", {"start": v(98.93, 44.73) * mm, "end": v(98.93, 36.82) * mm});
            skLineSegment(sketch, "E53.3.2.3", {"start": v(95.51, 36.82) * mm, "end": v(98.93, 36.82) * mm});
            skLineSegment(sketch, "E53.3.2.4", {"start": v(88.58, 35.55) * mm, "end": v(100.2, 35.55) * mm});
            skLineSegment(sketch, "E53.3.2.5", {"start": v(88.58, 55.82) * mm, "end": v(88.58, 35.55) * mm});
            skLineSegment(sketch, "E53.3.2.6", {"start": v(98.93, 46.64) * mm, "end": v(95.65, 46.64) * mm});
            skLineSegment(sketch, "E53.3.2.7", {"start": v(98.93, 44.73) * mm, "end": v(95.62, 44.73) * mm});
            skLineSegment(sketch, "E53.3.2.8", {"start": v(93.27, 54.55) * mm, "end": v(93.16, 46.64) * mm});
            skLineSegment(sketch, "E53.3.2.9", {"start": v(95.76, 54.55) * mm, "end": v(95.65, 46.64) * mm});
            skLineSegment(sketch, "E53.3.2.10", {"start": v(98.93, 54.55) * mm, "end": v(98.93, 46.64) * mm});
            skLineSegment(sketch, "E53.3.2.11", {"start": v(89.85, 54.55) * mm, "end": v(89.85, 46.64) * mm});
            skLineSegment(sketch, "E53.3.2.12", {"start": v(89.85, 36.82) * mm, "end": v(93.02, 36.82) * mm});
            skLineSegment(sketch, "E53.3.2.13", {"start": v(89.85, 54.55) * mm, "end": v(93.27, 54.55) * mm});
            skLineSegment(sketch, "E53.3.2.14", {"start": v(95.62, 44.73) * mm, "end": v(95.51, 36.82) * mm});
            skLineSegment(sketch, "E53.3.2.15", {"start": v(93.13, 44.73) * mm, "end": v(89.85, 44.73) * mm});
            skLineSegment(sketch, "E53.3.2.16", {"start": v(93.13, 44.73) * mm, "end": v(93.02, 36.82) * mm});
            skLineSegment(sketch, "E53.3.2.17", {"start": v(88.58, 55.82) * mm, "end": v(100.2, 55.82) * mm});
            skLineSegment(sketch, "E53.3.2.18", {"start": v(100.2, 55.82) * mm, "end": v(100.2, 35.55) * mm});
            skLineSegment(sketch, "E53.3.2.19", {"start": v(93.16, 46.64) * mm, "end": v(89.85, 46.64) * mm});
            skPoint(sketch, "E53.3.2.20", {"position": v(98.93, 45.68) * mm});
            skPoint(sketch, "E53.3.2.21", {"position": v(94.4, 36.82) * mm});
            skLineSegment(sketch, "E53.3.2.22", {"start": v(89.85, 44.73) * mm, "end": v(89.85, 36.82) * mm});
            skPoint(sketch, "E53.3.2.23", {"position": v(94.4, 45.68) * mm});
            skPoint(sketch, "E53.3.2.24", {"position": v(94.4, 45.68) * mm});
            skPoint(sketch, "E53.3.3.0", {"position": v(94.4, 71.08) * mm});
            skLineSegment(sketch, "E53.3.3.1", {"start": v(95.76, 79.95) * mm, "end": v(98.93, 79.95) * mm});
            skLineSegment(sketch, "E53.3.3.2", {"start": v(98.93, 70.13) * mm, "end": v(98.93, 62.22) * mm});
            skLineSegment(sketch, "E53.3.3.3", {"start": v(95.51, 62.22) * mm, "end": v(98.93, 62.22) * mm});
            skLineSegment(sketch, "E53.3.3.4", {"start": v(88.58, 60.95) * mm, "end": v(100.2, 60.95) * mm});
            skLineSegment(sketch, "E53.3.3.5", {"start": v(88.58, 81.22) * mm, "end": v(88.58, 60.95) * mm});
            skLineSegment(sketch, "E53.3.3.6", {"start": v(98.93, 72.04) * mm, "end": v(95.65, 72.04) * mm});
            skLineSegment(sketch, "E53.3.3.7", {"start": v(98.93, 70.13) * mm, "end": v(95.62, 70.13) * mm});
            skLineSegment(sketch, "E53.3.3.8", {"start": v(93.27, 79.95) * mm, "end": v(93.16, 72.04) * mm});
            skLineSegment(sketch, "E53.3.3.9", {"start": v(95.76, 79.95) * mm, "end": v(95.65, 72.04) * mm});
            skLineSegment(sketch, "E53.3.3.10", {"start": v(98.93, 79.95) * mm, "end": v(98.93, 72.04) * mm});
            skLineSegment(sketch, "E53.3.3.11", {"start": v(89.85, 79.95) * mm, "end": v(89.85, 72.04) * mm});
            skLineSegment(sketch, "E53.3.3.12", {"start": v(89.85, 62.22) * mm, "end": v(93.02, 62.22) * mm});
            skLineSegment(sketch, "E53.3.3.13", {"start": v(89.85, 79.95) * mm, "end": v(93.27, 79.95) * mm});
            skLineSegment(sketch, "E53.3.3.14", {"start": v(95.62, 70.13) * mm, "end": v(95.51, 62.22) * mm});
            skLineSegment(sketch, "E53.3.3.15", {"start": v(93.13, 70.13) * mm, "end": v(89.85, 70.13) * mm});
            skLineSegment(sketch, "E53.3.3.16", {"start": v(93.13, 70.13) * mm, "end": v(93.02, 62.22) * mm});
            skLineSegment(sketch, "E53.3.3.17", {"start": v(88.58, 81.22) * mm, "end": v(100.2, 81.22) * mm});
            skLineSegment(sketch, "E53.3.3.18", {"start": v(100.2, 81.22) * mm, "end": v(100.2, 60.95) * mm});
            skLineSegment(sketch, "E53.3.3.19", {"start": v(93.16, 72.04) * mm, "end": v(89.85, 72.04) * mm});
            skPoint(sketch, "E53.3.3.20", {"position": v(98.93, 71.08) * mm});
            skPoint(sketch, "E53.3.3.21", {"position": v(94.4, 62.22) * mm});
            skLineSegment(sketch, "E53.3.3.22", {"start": v(89.85, 70.13) * mm, "end": v(89.85, 62.22) * mm});
            skPoint(sketch, "E53.3.3.23", {"position": v(94.4, 71.08) * mm});
            skPoint(sketch, "E53.3.3.24", {"position": v(94.4, 71.08) * mm});
            skPoint(sketch, "E53.4.0.0", {"position": v(119.28, -5.12) * mm});
            skLineSegment(sketch, "E53.4.0.1", {"start": v(120.65, 3.75) * mm, "end": v(123.82, 3.75) * mm});
            skLineSegment(sketch, "E53.4.0.2", {"start": v(123.82, -6.07) * mm, "end": v(123.82, -13.98) * mm});
            skLineSegment(sketch, "E53.4.0.3", {"start": v(120.4, -13.98) * mm, "end": v(123.82, -13.98) * mm});
            skLineSegment(sketch, "E53.4.0.4", {"start": v(113.48, -15.25) * mm, "end": v(125.1, -15.25) * mm});
            skLineSegment(sketch, "E53.4.0.5", {"start": v(113.48, 5.02) * mm, "end": v(113.48, -15.25) * mm});
            skLineSegment(sketch, "E53.4.0.6", {"start": v(123.82, -4.16) * mm, "end": v(120.54, -4.16) * mm});
            skLineSegment(sketch, "E53.4.0.7", {"start": v(123.82, -6.07) * mm, "end": v(120.51, -6.07) * mm});
            skLineSegment(sketch, "E53.4.0.8", {"start": v(118.16, 3.75) * mm, "end": v(118.05, -4.16) * mm});
            skLineSegment(sketch, "E53.4.0.9", {"start": v(120.65, 3.75) * mm, "end": v(120.54, -4.16) * mm});
            skLineSegment(sketch, "E53.4.0.10", {"start": v(123.82, 3.75) * mm, "end": v(123.82, -4.16) * mm});
            skLineSegment(sketch, "E53.4.0.11", {"start": v(114.75, 3.75) * mm, "end": v(114.75, -4.16) * mm});
            skLineSegment(sketch, "E53.4.0.12", {"start": v(114.75, -13.98) * mm, "end": v(117.92, -13.98) * mm});
            skLineSegment(sketch, "E53.4.0.13", {"start": v(114.75, 3.75) * mm, "end": v(118.16, 3.75) * mm});
            skLineSegment(sketch, "E53.4.0.14", {"start": v(120.51, -6.07) * mm, "end": v(120.4, -13.98) * mm});
            skLineSegment(sketch, "E53.4.0.15", {"start": v(118.03, -6.07) * mm, "end": v(114.75, -6.07) * mm});
            skLineSegment(sketch, "E53.4.0.16", {"start": v(118.03, -6.07) * mm, "end": v(117.92, -13.98) * mm});
            skLineSegment(sketch, "E53.4.0.17", {"start": v(113.48, 5.02) * mm, "end": v(125.1, 5.02) * mm});
            skLineSegment(sketch, "E53.4.0.18", {"start": v(125.1, 5.02) * mm, "end": v(125.1, -15.25) * mm});
            skLineSegment(sketch, "E53.4.0.19", {"start": v(118.05, -4.16) * mm, "end": v(114.75, -4.16) * mm});
            skPoint(sketch, "E53.4.0.20", {"position": v(123.82, -5.12) * mm});
            skPoint(sketch, "E53.4.0.21", {"position": v(119.28, -13.98) * mm});
            skLineSegment(sketch, "E53.4.0.22", {"start": v(114.75, -6.07) * mm, "end": v(114.75, -13.98) * mm});
            skPoint(sketch, "E53.4.0.23", {"position": v(119.28, -5.12) * mm});
            skPoint(sketch, "E53.4.0.24", {"position": v(119.28, -5.12) * mm});
            skPoint(sketch, "E53.4.1.0", {"position": v(119.28, 20.28) * mm});
            skLineSegment(sketch, "E53.4.1.1", {"start": v(120.65, 29.15) * mm, "end": v(123.82, 29.15) * mm});
            skLineSegment(sketch, "E53.4.1.2", {"start": v(123.82, 19.33) * mm, "end": v(123.82, 11.42) * mm});
            skLineSegment(sketch, "E53.4.1.3", {"start": v(120.4, 11.42) * mm, "end": v(123.82, 11.42) * mm});
            skLineSegment(sketch, "E53.4.1.4", {"start": v(113.48, 10.15) * mm, "end": v(125.1, 10.15) * mm});
            skLineSegment(sketch, "E53.4.1.5", {"start": v(113.48, 30.42) * mm, "end": v(113.48, 10.15) * mm});
            skLineSegment(sketch, "E53.4.1.6", {"start": v(123.82, 21.24) * mm, "end": v(120.54, 21.24) * mm});
            skLineSegment(sketch, "E53.4.1.7", {"start": v(123.82, 19.33) * mm, "end": v(120.51, 19.33) * mm});
            skLineSegment(sketch, "E53.4.1.8", {"start": v(118.16, 29.15) * mm, "end": v(118.05, 21.24) * mm});
            skLineSegment(sketch, "E53.4.1.9", {"start": v(120.65, 29.15) * mm, "end": v(120.54, 21.24) * mm});
            skLineSegment(sketch, "E53.4.1.10", {"start": v(123.82, 29.15) * mm, "end": v(123.82, 21.24) * mm});
            skLineSegment(sketch, "E53.4.1.11", {"start": v(114.75, 29.15) * mm, "end": v(114.75, 21.24) * mm});
            skLineSegment(sketch, "E53.4.1.12", {"start": v(114.75, 11.42) * mm, "end": v(117.92, 11.42) * mm});
            skLineSegment(sketch, "E53.4.1.13", {"start": v(114.75, 29.15) * mm, "end": v(118.16, 29.15) * mm});
            skLineSegment(sketch, "E53.4.1.14", {"start": v(120.51, 19.33) * mm, "end": v(120.4, 11.42) * mm});
            skLineSegment(sketch, "E53.4.1.15", {"start": v(118.03, 19.33) * mm, "end": v(114.75, 19.33) * mm});
            skLineSegment(sketch, "E53.4.1.16", {"start": v(118.03, 19.33) * mm, "end": v(117.92, 11.42) * mm});
            skLineSegment(sketch, "E53.4.1.17", {"start": v(113.48, 30.42) * mm, "end": v(125.1, 30.42) * mm});
            skLineSegment(sketch, "E53.4.1.18", {"start": v(125.1, 30.42) * mm, "end": v(125.1, 10.15) * mm});
            skLineSegment(sketch, "E53.4.1.19", {"start": v(118.05, 21.24) * mm, "end": v(114.75, 21.24) * mm});
            skPoint(sketch, "E53.4.1.20", {"position": v(123.82, 20.28) * mm});
            skPoint(sketch, "E53.4.1.21", {"position": v(119.28, 11.42) * mm});
            skLineSegment(sketch, "E53.4.1.22", {"start": v(114.75, 19.33) * mm, "end": v(114.75, 11.42) * mm});
            skPoint(sketch, "E53.4.1.23", {"position": v(119.28, 20.28) * mm});
            skPoint(sketch, "E53.4.1.24", {"position": v(119.28, 20.28) * mm});
            skPoint(sketch, "E53.4.2.0", {"position": v(119.28, 45.68) * mm});
            skLineSegment(sketch, "E53.4.2.1", {"start": v(120.65, 54.55) * mm, "end": v(123.82, 54.55) * mm});
            skLineSegment(sketch, "E53.4.2.2", {"start": v(123.82, 44.73) * mm, "end": v(123.82, 36.82) * mm});
            skLineSegment(sketch, "E53.4.2.3", {"start": v(120.4, 36.82) * mm, "end": v(123.82, 36.82) * mm});
            skLineSegment(sketch, "E53.4.2.4", {"start": v(113.48, 35.55) * mm, "end": v(125.1, 35.55) * mm});
            skLineSegment(sketch, "E53.4.2.5", {"start": v(113.48, 55.82) * mm, "end": v(113.48, 35.55) * mm});
            skLineSegment(sketch, "E53.4.2.6", {"start": v(123.82, 46.64) * mm, "end": v(120.54, 46.64) * mm});
            skLineSegment(sketch, "E53.4.2.7", {"start": v(123.82, 44.73) * mm, "end": v(120.51, 44.73) * mm});
            skLineSegment(sketch, "E53.4.2.8", {"start": v(118.16, 54.55) * mm, "end": v(118.05, 46.64) * mm});
            skLineSegment(sketch, "E53.4.2.9", {"start": v(120.65, 54.55) * mm, "end": v(120.54, 46.64) * mm});
            skLineSegment(sketch, "E53.4.2.10", {"start": v(123.82, 54.55) * mm, "end": v(123.82, 46.64) * mm});
            skLineSegment(sketch, "E53.4.2.11", {"start": v(114.75, 54.55) * mm, "end": v(114.75, 46.64) * mm});
            skLineSegment(sketch, "E53.4.2.12", {"start": v(114.75, 36.82) * mm, "end": v(117.92, 36.82) * mm});
            skLineSegment(sketch, "E53.4.2.13", {"start": v(114.75, 54.55) * mm, "end": v(118.16, 54.55) * mm});
            skLineSegment(sketch, "E53.4.2.14", {"start": v(120.51, 44.73) * mm, "end": v(120.4, 36.82) * mm});
            skLineSegment(sketch, "E53.4.2.15", {"start": v(118.03, 44.73) * mm, "end": v(114.75, 44.73) * mm});
            skLineSegment(sketch, "E53.4.2.16", {"start": v(118.03, 44.73) * mm, "end": v(117.92, 36.82) * mm});
            skLineSegment(sketch, "E53.4.2.17", {"start": v(113.48, 55.82) * mm, "end": v(125.1, 55.82) * mm});
            skLineSegment(sketch, "E53.4.2.18", {"start": v(125.1, 55.82) * mm, "end": v(125.1, 35.55) * mm});
            skLineSegment(sketch, "E53.4.2.19", {"start": v(118.05, 46.64) * mm, "end": v(114.75, 46.64) * mm});
            skPoint(sketch, "E53.4.2.20", {"position": v(123.82, 45.68) * mm});
            skPoint(sketch, "E53.4.2.21", {"position": v(119.28, 36.82) * mm});
            skLineSegment(sketch, "E53.4.2.22", {"start": v(114.75, 44.73) * mm, "end": v(114.75, 36.82) * mm});
            skPoint(sketch, "E53.4.2.23", {"position": v(119.28, 45.68) * mm});
            skPoint(sketch, "E53.4.2.24", {"position": v(119.28, 45.68) * mm});
            skPoint(sketch, "E53.4.3.0", {"position": v(119.28, 71.08) * mm});
            skLineSegment(sketch, "E53.4.3.1", {"start": v(120.65, 79.95) * mm, "end": v(123.82, 79.95) * mm});
            skLineSegment(sketch, "E53.4.3.2", {"start": v(123.82, 70.13) * mm, "end": v(123.82, 62.22) * mm});
            skLineSegment(sketch, "E53.4.3.3", {"start": v(120.4, 62.22) * mm, "end": v(123.82, 62.22) * mm});
            skLineSegment(sketch, "E53.4.3.4", {"start": v(113.48, 60.95) * mm, "end": v(125.1, 60.95) * mm});
            skLineSegment(sketch, "E53.4.3.5", {"start": v(113.48, 81.22) * mm, "end": v(113.48, 60.95) * mm});
            skLineSegment(sketch, "E53.4.3.6", {"start": v(123.82, 72.04) * mm, "end": v(120.54, 72.04) * mm});
            skLineSegment(sketch, "E53.4.3.7", {"start": v(123.82, 70.13) * mm, "end": v(120.51, 70.13) * mm});
            skLineSegment(sketch, "E53.4.3.8", {"start": v(118.16, 79.95) * mm, "end": v(118.05, 72.04) * mm});
            skLineSegment(sketch, "E53.4.3.9", {"start": v(120.65, 79.95) * mm, "end": v(120.54, 72.04) * mm});
            skLineSegment(sketch, "E53.4.3.10", {"start": v(123.82, 79.95) * mm, "end": v(123.82, 72.04) * mm});
            skLineSegment(sketch, "E53.4.3.11", {"start": v(114.75, 79.95) * mm, "end": v(114.75, 72.04) * mm});
            skLineSegment(sketch, "E53.4.3.12", {"start": v(114.75, 62.22) * mm, "end": v(117.92, 62.22) * mm});
            skLineSegment(sketch, "E53.4.3.13", {"start": v(114.75, 79.95) * mm, "end": v(118.16, 79.95) * mm});
            skLineSegment(sketch, "E53.4.3.14", {"start": v(120.51, 70.13) * mm, "end": v(120.4, 62.22) * mm});
            skLineSegment(sketch, "E53.4.3.15", {"start": v(118.03, 70.13) * mm, "end": v(114.75, 70.13) * mm});
            skLineSegment(sketch, "E53.4.3.16", {"start": v(118.03, 70.13) * mm, "end": v(117.92, 62.22) * mm});
            skLineSegment(sketch, "E53.4.3.17", {"start": v(113.48, 81.22) * mm, "end": v(125.1, 81.22) * mm});
            skLineSegment(sketch, "E53.4.3.18", {"start": v(125.1, 81.22) * mm, "end": v(125.1, 60.95) * mm});
            skLineSegment(sketch, "E53.4.3.19", {"start": v(118.05, 72.04) * mm, "end": v(114.75, 72.04) * mm});
            skPoint(sketch, "E53.4.3.20", {"position": v(123.82, 71.08) * mm});
            skPoint(sketch, "E53.4.3.21", {"position": v(119.28, 62.22) * mm});
            skLineSegment(sketch, "E53.4.3.22", {"start": v(114.75, 70.13) * mm, "end": v(114.75, 62.22) * mm});
            skPoint(sketch, "E53.4.3.23", {"position": v(119.28, 71.08) * mm});
            skPoint(sketch, "E53.4.3.24", {"position": v(119.28, 71.08) * mm});
            skLineSegment(sketch, "E53.direction1", {"start": v(13.9, -15.25) * mm, "end": v(38.8, -15.25) * mm, "construction": true});
            skLineSegment(sketch, "E53.direction2", {"start": v(13.9, -15.25) * mm, "end": v(13.9, 10.15) * mm, "construction": true});
            skSolve(sketch);
        }
        {
            var Q0;
            Q0=makeQuery(id+"F18.imprint","IMPRINT",FACE,{"disambiguationData":[TD([[makeQuery(id+"F18.imprint","IMPRINT",EDGE,{"derivedFrom":sQuery(id+"F18.wireOp",EDGE,"E53.1.3.1")}),1.0]])]});
            var Q1;
            Q1=makeQuery(id+"F18.imprint","IMPRINT",FACE,{"disambiguationData":[TD([[makeQuery(id+"F18.imprint","IMPRINT",EDGE,{"derivedFrom":sQuery(id+"F18.wireOp",EDGE,"E53.2.3.1")}),1.0]])]});
            var Q2;
            Q2=makeQuery(id+"F18.imprint","IMPRINT",FACE,{"disambiguationData":[TD([[makeQuery(id+"F18.imprint","IMPRINT",EDGE,{"derivedFrom":sQuery(id+"F18.wireOp",EDGE,"E53.2.2.1")}),1.0]])]});
            var Q3;
            Q3=makeQuery(id+"F18.imprint","IMPRINT",FACE,{"disambiguationData":[TD([[makeQuery(id+"F18.imprint","IMPRINT",EDGE,{"derivedFrom":sQuery(id+"F18.wireOp",EDGE,"E53.1.2.1")}),1.0]])]});
            var Q4;
            Q4=makeQuery(id+"F18.imprint","IMPRINT",FACE,{"disambiguationData":[TD([[makeQuery(id+"F18.imprint","IMPRINT",EDGE,{"derivedFrom":sQuery(id+"F18.wireOp",EDGE,"E53.0.3.1")}),1.0]])]});
            var Q5;
            Q5=makeQuery(id+"F18.imprint","IMPRINT",FACE,{"disambiguationData":[TD([[makeQuery(id+"F18.imprint","IMPRINT",EDGE,{"derivedFrom":sQuery(id+"F18.wireOp",EDGE,"E53.3.3.1")}),1.0]])]});
            var Q6;
            Q6=makeQuery(id+"F18.imprint","IMPRINT",FACE,{"disambiguationData":[TD([[makeQuery(id+"F18.imprint","IMPRINT",EDGE,{"derivedFrom":sQuery(id+"F18.wireOp",EDGE,"E53.0.2.1")}),1.0]])]});
            var Q7;
            Q7=makeQuery(id+"F18.imprint","IMPRINT",FACE,{"disambiguationData":[TD([[makeQuery(id+"F18.imprint","IMPRINT",EDGE,{"derivedFrom":sQuery(id+"F18.wireOp",EDGE,"E53.0.1.1")}),1.0]])]});
            var Q8;
            Q8=makeQuery(id+"F18.imprint","IMPRINT",FACE,{"disambiguationData":[TD([[makeQuery(id+"F18.imprint","IMPRINT",EDGE,{"derivedFrom":sQuery(id+"F18.wireOp",EDGE,"E53.1.1.1")}),1.0]])]});
            var Q9;
            Q9=makeQuery(id+"F18.imprint","IMPRINT",FACE,{"disambiguationData":[TD([[makeQuery(id+"F18.imprint","IMPRINT",EDGE,{"derivedFrom":sQuery(id+"F18.wireOp",EDGE,"E53.1.0.1")}),1.0]])]});
            var Q10;
            Q10=makeQuery(id+"F18.imprint","IMPRINT",FACE,{"disambiguationData":[TD([[makeQuery(id+"F18.imprint","IMPRINT",EDGE,{"derivedFrom":sQuery(id+"F18.wireOp",EDGE,"E40.bottom")}),1.0]])]});
            var Q11;
            Q11=makeQuery(id+"F18.imprint","IMPRINT",FACE,{"disambiguationData":[TD([[makeQuery(id+"F18.imprint","IMPRINT",EDGE,{"derivedFrom":sQuery(id+"F18.wireOp",EDGE,"E53.2.0.1")}),1.0]])]});
            var Q12;
            Q12=makeQuery(id+"F18.imprint","IMPRINT",FACE,{"disambiguationData":[TD([[makeQuery(id+"F18.imprint","IMPRINT",EDGE,{"derivedFrom":sQuery(id+"F18.wireOp",EDGE,"E53.3.0.1")}),1.0]])]});
            var Q13;
            Q13=makeQuery(id+"F18.imprint","IMPRINT",FACE,{"disambiguationData":[TD([[makeQuery(id+"F18.imprint","IMPRINT",EDGE,{"derivedFrom":sQuery(id+"F18.wireOp",EDGE,"E53.3.1.1")}),1.0]])]});
            var Q14;
            Q14=makeQuery(id+"F18.imprint","IMPRINT",FACE,{"disambiguationData":[TD([[makeQuery(id+"F18.imprint","IMPRINT",EDGE,{"derivedFrom":sQuery(id+"F18.wireOp",EDGE,"E53.2.1.1")}),1.0]])]});
            var Q15;
            Q15=makeQuery(id+"F18.imprint","IMPRINT",FACE,{"disambiguationData":[TD([[makeQuery(id+"F18.imprint","IMPRINT",EDGE,{"derivedFrom":sQuery(id+"F18.wireOp",EDGE,"E53.4.0.1")}),1.0]])]});
            var Q16;
            Q16=makeQuery(id+"F18.imprint","IMPRINT",FACE,{"disambiguationData":[TD([[makeQuery(id+"F18.imprint","IMPRINT",EDGE,{"derivedFrom":sQuery(id+"F18.wireOp",EDGE,"E53.4.1.1")}),1.0]])]});
            var Q17;
            Q17=makeQuery(id+"F18.imprint","IMPRINT",FACE,{"disambiguationData":[TD([[makeQuery(id+"F18.imprint","IMPRINT",EDGE,{"derivedFrom":sQuery(id+"F18.wireOp",EDGE,"E53.4.2.1")}),1.0]])]});
            var Q18;
            Q18=makeQuery(id+"F18.imprint","IMPRINT",FACE,{"disambiguationData":[TD([[makeQuery(id+"F18.imprint","IMPRINT",EDGE,{"derivedFrom":sQuery(id+"F18.wireOp",EDGE,"E53.3.2.1")}),1.0]])]});
            var Q19;
            Q19=makeQuery(id+"F18.imprint","IMPRINT",FACE,{"disambiguationData":[TD([[makeQuery(id+"F18.imprint","IMPRINT",EDGE,{"derivedFrom":sQuery(id+"F18.wireOp",EDGE,"E53.4.3.1")}),1.0]])]});
            extrude(context, id + "F19", {"entities" : qUnion([Q0, Q1, Q2, Q3, Q4, Q5, Q6, Q7, Q8, Q9, Q10, Q11, Q12, Q13, Q14, Q15, Q16, Q17, Q18, Q19]), "depth" : 0.5 * mm, "offsetDistance" : 25.4 * mm});
        }
        {
            var Q0;
            {var subQ0=sQuery(id+"F0.wireOp",EDGE,"E0.bottom");var subQ1=sQuery(id+"F0.wireOp",EDGE,"E3");var subQ2=sQuery(id+"F0.wireOp",EDGE,"E1.top");var subQ3=sQuery(id+"F0.wireOp",EDGE,"E2");Q0=makeQuery(id+"F12.boolean.opBoolean","SPLIT",FACE,{"disambiguationData":[TD([makeQuery(id+"F7.opExtrude","SWEPT_FACE",FACE,{"disambiguationData":[OSD([subQ0])]})])],"derivedFrom":makeQuery(id+"F7.opExtrude","CAP_FACE",FACE,{"disambiguationData":[OSD([subQ0,subQ2,subQ3,subQ1])],"isStart":false})});}
            var sketch = newSketch(context, id + "F20", { "sketchPlane" : qUnion([Q0])});
            skLineSegment(sketch, "E54", {"start": v(3.66, -48.3) * mm, "end": v(3.66, -32.42) * mm, "construction": true});
            skLineSegment(sketch, "E55.bottom", {"start": v(22.71, -48.3) * mm, "end": v(-15.39, -48.3) * mm});
            skLineSegment(sketch, "E55.top", {"start": v(22.71, -16.54) * mm, "end": v(-15.39, -16.54) * mm});
            skLineSegment(sketch, "E55.left", {"start": v(22.71, -48.3) * mm, "end": v(22.71, -16.54) * mm});
            skLineSegment(sketch, "E55.right", {"start": v(-15.39, -48.3) * mm, "end": v(-15.39, -16.54) * mm});
            skPoint(sketch, "E55.middle", {"position": v(3.66, -32.42) * mm});
            skLineSegment(sketch, "E56", {"start": v(3.66, -16.54) * mm, "end": v(3.66, -48.3) * mm});
            skLineSegment(sketch, "E57.bottom", {"start": v(-2.94, -22.02) * mm, "end": v(1.05, -22.02) * mm});
            skLineSegment(sketch, "E57.top", {"start": v(-2.94, -31.27) * mm, "end": v(1.05, -31.27) * mm});
            skLineSegment(sketch, "E57.left", {"start": v(-2.94, -22.02) * mm, "end": v(-2.94, -31.27) * mm});
            skLineSegment(sketch, "E57.right", {"start": v(1.05, -22.02) * mm, "end": v(1.05, -31.27) * mm});
            skLineSegment(sketch, "E58", {"start": v(2.67, -32.98) * mm, "end": v(0.7, -33.23) * mm});
            skLineSegment(sketch, "E59", {"start": v(0.7, -33.23) * mm, "end": v(0.77, -33.79) * mm});
            skLineSegment(sketch, "E60", {"start": v(0.77, -33.79) * mm, "end": v(2.75, -33.53) * mm});
            skLineSegment(sketch, "E61", {"start": v(2.75, -33.53) * mm, "end": v(2.67, -32.98) * mm});
            skLineSegment(sketch, "E62.MirrorCS", {"start": v(10.26, -22.02) * mm, "end": v(6.27, -22.02) * mm});
            skLineSegment(sketch, "E63.MirrorCS", {"start": v(10.26, -22.02) * mm, "end": v(10.26, -31.27) * mm});
            skLineSegment(sketch, "E64.MirrorCS", {"start": v(10.26, -31.27) * mm, "end": v(6.27, -31.27) * mm});
            skLineSegment(sketch, "E65.MirrorCS", {"start": v(6.27, -22.02) * mm, "end": v(6.27, -31.27) * mm});
            skLineSegment(sketch, "E66.MirrorCS", {"start": v(4.65, -32.98) * mm, "end": v(6.63, -33.23) * mm});
            skLineSegment(sketch, "E67.MirrorCS", {"start": v(6.63, -33.23) * mm, "end": v(6.56, -33.79) * mm});
            skLineSegment(sketch, "E68.MirrorCS", {"start": v(6.56, -33.79) * mm, "end": v(4.58, -33.53) * mm});
            skLineSegment(sketch, "E69.MirrorCS", {"start": v(4.58, -33.53) * mm, "end": v(4.65, -32.98) * mm});
            skSolve(sketch);
        }
        {
            var Q0;
            {var subQ0=sQuery(id+"F20.wireOp",EDGE,"E55.right");Q0=makeQuery(id+"F20.imprint","IMPRINT",FACE,{"disambiguationData":[TD([[makeQuery(id+"F20.imprint","IMPRINT",EDGE,{"derivedFrom":subQ0}),-1.0]])]});}
            var Q1;
            {var subQ0=sQuery(id+"F20.wireOp",EDGE,"E55.left");Q1=makeQuery(id+"F20.imprint","IMPRINT",FACE,{"disambiguationData":[TD([[makeQuery(id+"F20.imprint","IMPRINT",EDGE,{"derivedFrom":subQ0}),1.0]])]});}
            extrude(context, id + "F21", {"entities" : qUnion([Q0, Q1]), "operationType" : NewBodyOperationType.REMOVE, "oppositeDirection" : true, "depth" : 0.5 * mm, "offsetDistance" : 25.4 * mm});
        }
        {
            var Q0;
            {var subQ0=sQuery(id+"F0.wireOp",EDGE,"E0.bottom");var subQ1=sQuery(id+"F0.wireOp",EDGE,"E3");var subQ2=sQuery(id+"F0.wireOp",EDGE,"E1.top");var subQ3=sQuery(id+"F0.wireOp",EDGE,"E2");Q0=makeQuery(id+"F21.boolean.opBoolean","SPLIT",FACE,{"disambiguationData":[TD([makeQuery(id+"F21.opExtrude","SWEPT_FACE",FACE,{"disambiguationData":[OSD([sQuery(id+"F20.wireOp",EDGE,"E57.bottom")])]})])],"derivedFrom":makeQuery(id+"F12.boolean.opBoolean","SPLIT",FACE,{"disambiguationData":[TD([makeQuery(id+"F7.opExtrude","SWEPT_FACE",FACE,{"disambiguationData":[OSD([subQ0])]})])],"derivedFrom":makeQuery(id+"F7.opExtrude","CAP_FACE",FACE,{"disambiguationData":[OSD([subQ0,subQ2,subQ3,subQ1])],"isStart":false})})});}
            var Q1;
            {var subQ0=sQuery(id+"F0.wireOp",EDGE,"E0.bottom");var subQ1=sQuery(id+"F0.wireOp",EDGE,"E3");var subQ2=sQuery(id+"F0.wireOp",EDGE,"E1.top");var subQ3=sQuery(id+"F0.wireOp",EDGE,"E2");Q1=makeQuery(id+"F21.boolean.opBoolean","SPLIT",FACE,{"disambiguationData":[TD([makeQuery(id+"F21.opExtrude","SWEPT_FACE",FACE,{"disambiguationData":[OSD([sQuery(id+"F20.wireOp",EDGE,"E62.MirrorCS")])]})])],"derivedFrom":makeQuery(id+"F12.boolean.opBoolean","SPLIT",FACE,{"disambiguationData":[TD([makeQuery(id+"F7.opExtrude","SWEPT_FACE",FACE,{"disambiguationData":[OSD([subQ0])]})])],"derivedFrom":makeQuery(id+"F7.opExtrude","CAP_FACE",FACE,{"disambiguationData":[OSD([subQ0,subQ2,subQ3,subQ1])],"isStart":false})})});}
            extrude(context, id + "F22", {"entities" : qUnion([Q0, Q1]), "operationType" : NewBodyOperationType.REMOVE, "oppositeDirection" : true, "depth" : 0.56 * mm, "offsetDistance" : 25.4 * mm});
        }
        {
            var Q0;
            Q0=makeQuery(id+"F14.opExtrude","CAP_FACE",FACE,{"disambiguationData":[OSD([sQuery(id+"F13.wireOp",EDGE,"E16.top"),sQuery(id+"F13.wireOp",EDGE,"E16.left"),sQuery(id+"F13.wireOp",EDGE,"E16.right"),sQuery(id+"F13.wireOp",EDGE,"E22"),sQuery(id+"F13.wireOp",EDGE,"E23"),sQuery(id+"F13.wireOp",EDGE,"E24"),sQuery(id+"F13.wireOp",EDGE,"E25")])],"isStart":true});
            var sketch = newSketch(context, id + "F23", { "sketchPlane" : qUnion([Q0])});
            skCircle(sketch, "E70.0", {"center": v(3.66, 66.88) * mm, "radius": 0.28 * mm});
            skCircle(sketch, "E71", {"center": v(3.66, 109.7) * mm, "radius": 3.18 * mm});
            skSolve(sketch);
        }
        {
            var Q0;
            Q0=makeQuery(id+"F23.imprint","IMPRINT",FACE,{"disambiguationData":[TD([[makeQuery(id+"F23.imprint","IMPRINT",EDGE,{"derivedFrom":sQuery(id+"F23.wireOp",EDGE,"E71")}),1.0]])]});
            extrude(context, id + "F24", {"entities" : qUnion([Q0]), "operationType" : NewBodyOperationType.ADD, "depth" : 7.37 * mm, "offsetDistance" : 25.4 * mm});
        }
        {
            var Q0;
            Q0=makeQuery(id+"F24.opExtrude","CAP_FACE",FACE,{"disambiguationData":[OSD([sQuery(id+"F23.wireOp",EDGE,"E71")])],"isStart":false});
            var sketch = newSketch(context, id + "F25", { "sketchPlane" : qUnion([Q0])});
            skCircle(sketch, "E72", {"center": v(3.66, 109.7) * mm, "radius": 4.45 * mm});
            skCircle(sketch, "E73", {"center": v(3.66, 109.7) * mm, "radius": 2.54 * mm});
            skSolve(sketch);
        }
        {
            var Q0;
            Q0=makeQuery(id+"F25.imprint","IMPRINT",FACE,{"disambiguationData":[TD([[makeQuery(id+"F25.imprint","IMPRINT",EDGE,{"derivedFrom":sQuery(id+"F25.wireOp",EDGE,"E72")}),1.0]])]});
            var Q1;
            Q1=makeQuery(id+"F25.imprint","IMPRINT",FACE,{"disambiguationData":[TD([[makeQuery(id+"F25.imprint","IMPRINT",EDGE,{"derivedFrom":sQuery(id+"F25.wireOp",EDGE,"E73")}),-1.0]])]});
            extrude(context, id + "F26", {"entities" : qUnion([Q0, Q1]), "operationType" : NewBodyOperationType.ADD, "depth" : 12.7 * mm, "offsetDistance" : 25.4 * mm});
        }
        {
            var Q0;
            Q0=makeQuery(id+"F26.opExtrude","CAP_FACE",FACE,{"disambiguationData":[OSD([sQuery(id+"F25.wireOp",EDGE,"E72"),sQuery(id+"F25.wireOp",EDGE,"E73")])],"isStart":false});
            var sketch = newSketch(context, id + "F27", { "sketchPlane" : qUnion([Q0])});
            skCircle(sketch, "E74", {"center": v(3.66, 109.7) * mm, "radius": 3.81 * mm});
            skCircle(sketch, "E75", {"center": v(3.66, 109.7) * mm, "radius": 3.18 * mm});
            skSolve(sketch);
        }
        {
            var Q0;
            Q0=makeQuery(id+"F27.imprint","IMPRINT",FACE,{"disambiguationData":[TD([[makeQuery(id+"F27.imprint","IMPRINT",EDGE,{"derivedFrom":sQuery(id+"F27.wireOp",EDGE,"E74")}),1.0]])]});
            var Q1;
            Q1=makeQuery(id+"F27.imprint","IMPRINT",FACE,{"disambiguationData":[TD([[makeQuery(id+"F27.imprint","IMPRINT",EDGE,{"derivedFrom":makeQuery(id+"F26.opExtrude","CAP_EDGE",EDGE,{"disambiguationData":[OSD([sQuery(id+"F25.wireOp",EDGE,"E73")])],"isStart":false})}),1.0]])]});
            var Q2;
            Q2=makeQuery(id+"F27.imprint","IMPRINT",FACE,{"disambiguationData":[TD([[makeQuery(id+"F27.imprint","IMPRINT",EDGE,{"derivedFrom":sQuery(id+"F27.wireOp",EDGE,"E75")}),1.0]])]});
            extrude(context, id + "F28", {"entities" : qUnion([Q0, Q1, Q2]), "operationType" : NewBodyOperationType.ADD, "depth" : 10.16 * mm, "offsetDistance" : 25.4 * mm});
        }
        {
            var Q0;
            Q0=makeQuery(id+"F28.opExtrude","CAP_FACE",FACE,{"disambiguationData":[OSD([sQuery(id+"F27.wireOp",EDGE,"E74"),sQuery(id+"F27.wireOp",EDGE,"E75")])],"isStart":false});
            var sketch = newSketch(context, id + "F29", { "sketchPlane" : qUnion([Q0])});
            skCircle(sketch, "E76.0", {"center": v(3.66, 109.7) * mm, "radius": 5.08 * mm});
            skSolve(sketch);
        }
        {
            var Q0;
            Q0=makeQuery(id+"F29.imprint","IMPRINT",FACE,{"disambiguationData":[TD([[makeQuery(id+"F29.imprint","IMPRINT",EDGE,{"derivedFrom":sQuery(id+"F29.wireOp",EDGE,"E76.0")}),1.0]])]});
            cPlane(context, id + "F30", {"entities" : qUnion([Q0]), "cplaneType" : CPlaneType.OFFSET, "offset" : 25.4 * mm, "width" : 152.4 * mm, "height" : 152.4 * mm});
        }
        {
            var Q0;
            Q0=makeQuery(id+"F29.imprint","IMPRINT",FACE,{"disambiguationData":[TD([[makeQuery(id+"F29.imprint","IMPRINT",EDGE,{"derivedFrom":sQuery(id+"F29.wireOp",EDGE,"E76.0")}),1.0]])]});
            cPlane(context, id + "F31", {"entities" : qUnion([Q0]), "cplaneType" : CPlaneType.OFFSET, "offset" : 12.7 * mm, "width" : 152.4 * mm, "height" : 152.4 * mm});
        }
        {
            var Q0;
            Q0=qCreatedBy(id+"F31.planeOp",FACE);
            var sketch = newSketch(context, id + "F32", { "sketchPlane" : qUnion([Q0])});
            skPoint(sketch, "E77.0", {"position": v(3.66, 109.7) * mm});
            skCircle(sketch, "E78", {"center": v(3.66, 109.7) * mm, "radius": 5.72 * mm});
            skSolve(sketch);
        }
        {
            var Q0;
            Q0=qCreatedBy(id+"F30.planeOp",FACE);
            var sketch = newSketch(context, id + "F33", { "sketchPlane" : qUnion([Q0])});
            skPoint(sketch, "E79.0", {"position": v(3.66, 109.7) * mm});
            skCircle(sketch, "E80", {"center": v(3.66, 109.7) * mm, "radius": 6.35 * mm});
            skSolve(sketch);
        }
        {
            var Q0;
            Q0=makeQuery(id+"F29.imprint","IMPRINT",FACE,{"disambiguationData":[TD([[makeQuery(id+"F29.imprint","IMPRINT",EDGE,{"derivedFrom":makeQuery(id+"F28.opExtrude","CAP_EDGE",EDGE,{"disambiguationData":[OSD([sQuery(id+"F27.wireOp",EDGE,"E74")])],"isStart":false})}),1.0]])]});
            cPlane(context, id + "F34", {"entities" : qUnion([Q0]), "cplaneType" : CPlaneType.OFFSET, "offset" : 0.2 * mm, "width" : 152.4 * mm, "height" : 152.4 * mm});
        }
        {
            var Q0;
            Q0=qCreatedBy(id+"F34.planeOp",FACE);
            var sketch = newSketch(context, id + "F35", { "sketchPlane" : qUnion([Q0])});
            skPoint(sketch, "E81.0", {"position": v(3.66, 109.7) * mm});
            skCircle(sketch, "E82", {"center": v(3.66, 109.7) * mm, "radius": 5.08 * mm});
            skSolve(sketch);
        }
        {
            var Q0;
            Q0=makeQuery(id+"F35.imprint","IMPRINT",FACE,{"disambiguationData":[TD([[makeQuery(id+"F35.imprint","IMPRINT",EDGE,{"derivedFrom":sQuery(id+"F35.wireOp",EDGE,"E82")}),1.0]])]});
            var Q1;
            Q1=makeQuery(id+"F33.imprint","IMPRINT",FACE,{"disambiguationData":[TD([[makeQuery(id+"F33.imprint","IMPRINT",EDGE,{"derivedFrom":sQuery(id+"F33.wireOp",EDGE,"E80")}),1.0]])]});
            loft(context, id + "F36", {"sheetProfilesArray" : [{ "sheetProfileEntities" : qUnion([Q0]) }, { "sheetProfileEntities" : qUnion([Q1]) }]});
        }
        {
            var Q0;
            Q0=makeQuery(id+"F36.opLoft","CAP_FACE",FACE,{"disambiguationData":[OSD([makeQuery(id+"F35.imprint","IMPRINT",FACE,{"disambiguationData":[TD([[makeQuery(id+"F35.imprint","IMPRINT",EDGE,{"derivedFrom":sQuery(id+"F35.wireOp",EDGE,"E82")}),1.0]])]})])],"isStart":true});
            extrude(context, id + "F37", {"entities" : qUnion([Q0]), "operationType" : NewBodyOperationType.ADD, "depth" : 0.23 * mm, "offsetDistance" : 25.4 * mm});
        }
        {
            var Q0;
            Q0=qCreatedBy(id+"F30.planeOp",FACE);
            var sketch = newSketch(context, id + "F38", { "sketchPlane" : qUnion([Q0])});
            skPoint(sketch, "E83.0", {"position": v(3.66, 109.7) * mm});
            skCircle(sketch, "E84", {"center": v(3.66, 109.7) * mm, "radius": 5.13 * mm});
            skSolve(sketch);
        }
        {
            var Q0;
            Q0=sQuery(id+"F38.wireOp",VERTEX,"E83.0");
            var Q1;
            Q1=makeQuery(id+"F19.opExtrude","SWEPT_BODY",BODY,{"disambiguationData":[OSD([sQuery(id+"F18.wireOp",EDGE,"E40.bottom"),sQuery(id+"F18.wireOp",EDGE,"E40.top"),sQuery(id+"F18.wireOp",EDGE,"E40.left"),sQuery(id+"F18.wireOp",EDGE,"E40.right"),sQuery(id+"F18.wireOp",EDGE,"E42.left"),sQuery(id+"F18.wireOp",EDGE,"E42.right"),sQuery(id+"F18.wireOp",EDGE,"E43.bottom"),sQuery(id+"F18.wireOp",EDGE,"E43.top"),sQuery(id+"F18.wireOp",EDGE,"E44.0"),sQuery(id+"F18.wireOp",EDGE,"E44.1"),sQuery(id+"F18.wireOp",EDGE,"E44.2"),sQuery(id+"F18.wireOp",EDGE,"E44.3"),sQuery(id+"F18.wireOp",EDGE,"E45.trimOffspring"),sQuery(id+"F18.wireOp",EDGE,"E46.trimOffspring"),sQuery(id+"F18.wireOp",EDGE,"E47.trimOffspring"),sQuery(id+"F18.wireOp",EDGE,"E48.trimOffspring"),sQuery(id+"F18.wireOp",EDGE,"E49.trimOffspring"),sQuery(id+"F18.wireOp",EDGE,"E50.trimOffspring"),sQuery(id+"F18.wireOp",EDGE,"E51.trimOffspring"),sQuery(id+"F18.wireOp",EDGE,"E52.trimOffspring")])]});
            hole(context, id + "F39", {"style" : HoleStyle.SIMPLE, "endStyle" : HoleEndStyle.BLIND, "holeDiameter" : 8.9 * mm, "holeDepth" : 12.7 * mm, "isTappedThrough" : true, "tappedDepth" : 12.7 * mm, "tapClearance" : 3, "locations" : qUnion([Q0]), "scope" : qUnion([Q1])});
        }
        {
            var Q0;
            Q0=makeQuery(id+"F36.opLoft","CAP_FACE",FACE,{"disambiguationData":[OSD([makeQuery(id+"F33.imprint","IMPRINT",FACE,{"disambiguationData":[TD([[makeQuery(id+"F33.imprint","IMPRINT",EDGE,{"derivedFrom":sQuery(id+"F33.wireOp",EDGE,"E80")}),1.0]])]})])],"isStart":true});
            cPlane(context, id + "F40", {"entities" : qUnion([Q0]), "cplaneType" : CPlaneType.OFFSET, "offset" : 12.7 * mm, "oppositeDirection" : true, "width" : 152.4 * mm, "height" : 152.4 * mm});
        }
        {
            var Q0;
            Q0=qCreatedBy(id+"F40.planeOp",FACE);
            var sketch = newSketch(context, id + "F41", { "sketchPlane" : qUnion([Q0])});
            skPoint(sketch, "E85.0", {"position": v(3.66, 109.7) * mm});
            skCircle(sketch, "E86", {"center": v(3.66, 109.7) * mm, "radius": 4.45 * mm});
            skSolve(sketch);
        }
        {
            var Q0;
            Q0=qSketchRegion(id+"F41",true);
            extrude(context, id + "F42", {"entities" : qUnion([Q0]), "operationType" : NewBodyOperationType.ADD, "depth" : 12.83 * mm, "offsetDistance" : 25.4 * mm});
        }
        {
            var Q0;
            Q0=makeQuery(id+"F42.opExtrude","CAP_EDGE",EDGE,{"disambiguationData":[OSD([sQuery(id+"F41.wireOp",EDGE,"E86")])],"isStart":false});
            fillet(context, id + "F43", {"entities" : qUnion([Q0]), "radius" : 50.84 * mm, "tangentPropagation" : true, "allowEdgeOverflow" : false});
        }
        {
            var Q0;
            {var subQ1=sQuery(id+"F0.wireOp",EDGE,"E0.bottom");var subQ2=makeQuery(id+"F7.opExtrude","SWEPT_FACE",FACE,{"disambiguationData":[OSD([subQ1])]});var subQ15=sQuery(id+"F0.wireOp",EDGE,"E3");var subQ22=sQuery(id+"F0.wireOp",EDGE,"E1.top");var subQ29=sQuery(id+"F0.wireOp",EDGE,"E2");Q0=makeQuery(id+"F21.boolean.opBoolean","SPLIT",FACE,{"disambiguationData":[TD([subQ2])],"derivedFrom":makeQuery(id+"F12.boolean.opBoolean","SPLIT",FACE,{"disambiguationData":[TD([subQ2])],"derivedFrom":makeQuery(id+"F7.opExtrude","CAP_FACE",FACE,{"disambiguationData":[OSD([subQ1,subQ22,subQ29,subQ15])],"isStart":false})})});}
            var sketch = newSketch(context, id + "F44", { "sketchPlane" : qUnion([Q0])});
            skLineSegment(sketch, "E87.0", {"start": v(22.71, -48.3) * mm, "end": v(-15.39, -48.3) * mm});
            skLineSegment(sketch, "E88", {"start": v(3.66, -16.54) * mm, "end": v(3.66, -48.3) * mm});
            skSolve(sketch);
        }
        {
            var Q0;
            {var subQ0=sQuery(id+"F44.wireOp",EDGE,"E88");Q0=makeQuery(id+"F44.imprint","IMPRINT",FACE,{"disambiguationData":[TD([[makeQuery(id+"F44.imprint","IMPRINT",EDGE,{"derivedFrom":subQ0}),1.0]])]});}
            extrude(context, id + "F45", {"entities" : qUnion([Q0]), "operationType" : NewBodyOperationType.ADD, "oppositeDirection" : true, "depth" : 25.4 * mm, "offsetDistance" : 25.4 * mm});
        }
    });
